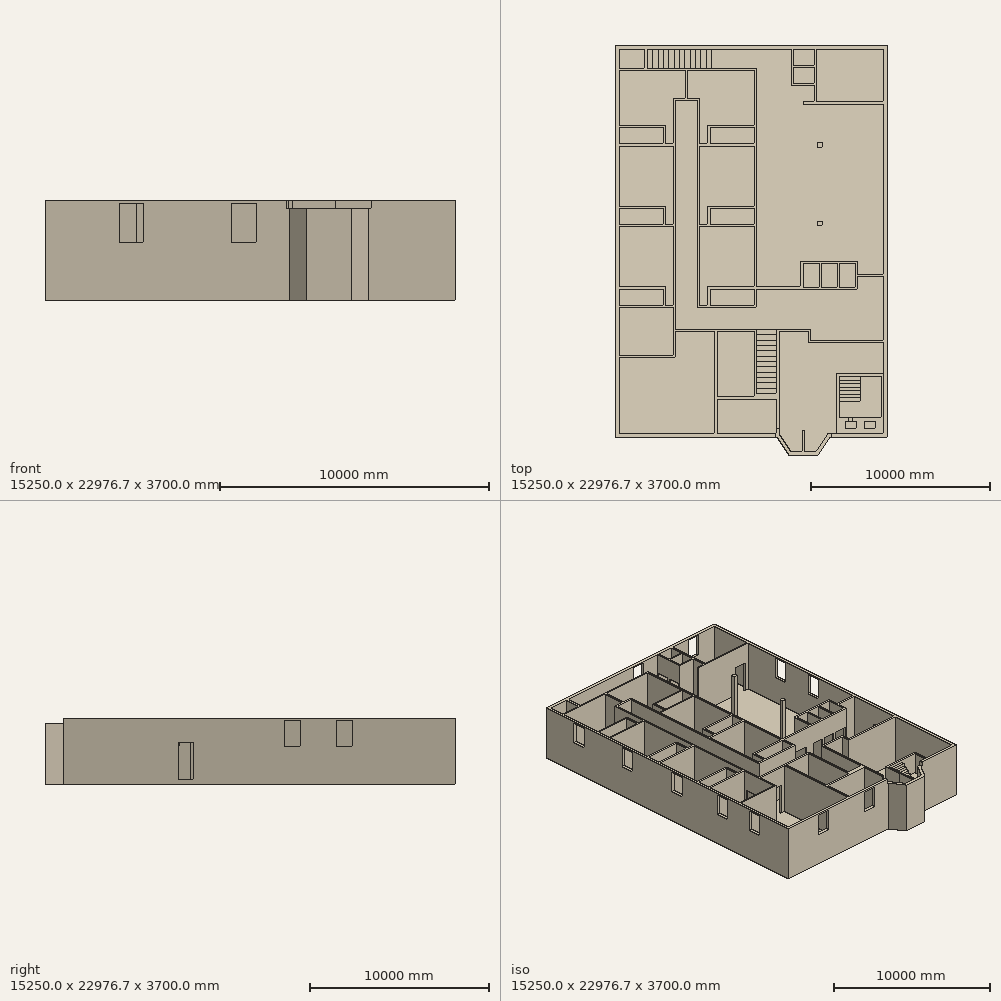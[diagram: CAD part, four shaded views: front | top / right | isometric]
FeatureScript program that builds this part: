
annotation { "Feature Type Name" : "Feature", "Feature Type Description" : "" }
export const myFeature = defineFeature(function(context is Context, id is Id, definition is map)
    precondition{}
    {
        {
            var Q0;
            Q0=qCreatedBy(makeId("Top.planeOp"),FACE);
            var sketch = newSketch(context, id + "F0", { "sketchPlane" : qUnion([Q0])});
            skLineSegment(sketch, "E0", {"start": v(-8625, -10471.67) * mm, "end": v(-8625, -7870.68) * mm});
            skLineSegment(sketch, "E1", {"start": v(-8625, 11488.33) * mm, "end": v(-949.17, 11488.33) * mm});
            skLineSegment(sketch, "E2", {"start": v(6625, 11488.33) * mm, "end": v(6625, 5731.46) * mm});
            skLineSegment(sketch, "E3", {"start": v(6625, -10471.67) * mm, "end": v(3405.76, -10471.67) * mm});
            skLineSegment(sketch, "E4", {"start": v(-8421.67, -10268.33) * mm, "end": v(-8421.67, -7870.68) * mm});
            skLineSegment(sketch, "E5", {"start": v(6421.67, 11285) * mm, "end": v(6421.67, 8336.67) * mm});
            skLineSegment(sketch, "E6", {"start": v(6421.67, -10268.33) * mm, "end": v(3295.42, -10268.33) * mm});
            skLineSegment(sketch, "E7", {"start": v(550.42, -4549.58) * mm, "end": v(550.42, -10268.33) * mm});
            skLineSegment(sketch, "E8", {"start": v(2634.58, -11285) * mm, "end": v(1973.75, -11285) * mm});
            skLineSegment(sketch, "E9", {"start": v(550.42, -10268.33) * mm, "end": v(1211.25, -11285) * mm});
            skLineSegment(sketch, "E10", {"start": v(3295.42, -10268.33) * mm, "end": v(2634.58, -11285) * mm});
            skLineSegment(sketch, "E11", {"start": v(440.07, -10471.67) * mm, "end": v(1100.9, -11488.33) * mm});
            skLineSegment(sketch, "E12", {"start": v(440.07, -10471.67) * mm, "end": v(-53.23, -10471.67) * mm});
            skLineSegment(sketch, "E13", {"start": v(2744.93, -11488.33) * mm, "end": v(1100.9, -11488.33) * mm});
            skLineSegment(sketch, "E14", {"start": v(423.33, -4422.5) * mm, "end": v(423.33, -8209.58) * mm});
            skLineSegment(sketch, "E15", {"start": v(1894.4, -2046.04) * mm, "end": v(1894.4, -724.38) * mm});
            skLineSegment(sketch, "E16", {"start": v(-720.42, -4422.5) * mm, "end": v(-720.42, -8209.58) * mm});
            skLineSegment(sketch, "E17", {"start": v(423.33, -8209.58) * mm, "end": v(-720.42, -8209.58) * mm});
            skLineSegment(sketch, "E18", {"start": v(423.33, -8336.67) * mm, "end": v(-1749.8, -8336.67) * mm});
            skLineSegment(sketch, "E19", {"start": v(-847.5, -4549.58) * mm, "end": v(-847.5, -8209.58) * mm});
            skLineSegment(sketch, "E20", {"start": v(423.33, -8336.67) * mm, "end": v(423.33, -10268.33) * mm});
            skLineSegment(sketch, "E21", {"start": v(-3046.04, -4549.58) * mm, "end": v(-3046.04, -10268.33) * mm});
            skLineSegment(sketch, "E22", {"start": v(-2918.96, -4549.58) * mm, "end": v(-2918.96, -8209.58) * mm});
            skLineSegment(sketch, "E23", {"start": v(-3046.04, -10268.33) * mm, "end": v(-4973.46, -10268.33) * mm});
            skLineSegment(sketch, "E24", {"start": v(-720.42, -4422.5) * mm, "end": v(-847.5, -4422.5) * mm});
            skLineSegment(sketch, "E25", {"start": v(-720.42, -3202.5) * mm, "end": v(-720.42, -2173.12) * mm});
            skLineSegment(sketch, "E26", {"start": v(-8421.67, 10192.08) * mm, "end": v(-720.42, 10192.08) * mm});
            skLineSegment(sketch, "E27", {"start": v(-8421.67, 10065) * mm, "end": v(-4698.12, 10065) * mm});
            skLineSegment(sketch, "E28", {"start": v(6421.67, -5159.58) * mm, "end": v(6421.67, -10268.33) * mm});
            skLineSegment(sketch, "E29", {"start": v(-8421.67, -3202.5) * mm, "end": v(-5371.67, -3202.5) * mm});
            skLineSegment(sketch, "E30", {"start": v(-847.5, -4422.5) * mm, "end": v(-1749.8, -4422.5) * mm});
            skLineSegment(sketch, "E31", {"start": v(-847.5, -4549.58) * mm, "end": v(-1749.8, -4549.58) * mm});
            skLineSegment(sketch, "E32", {"start": v(2634.58, 8336.67) * mm, "end": v(2634.58, 11285) * mm});
            skLineSegment(sketch, "E33", {"start": v(2507.5, 8336.67) * mm, "end": v(2507.5, 9251.67) * mm});
            skLineSegment(sketch, "E34", {"start": v(1351.04, 10268.33) * mm, "end": v(2507.5, 10268.33) * mm});
            skLineSegment(sketch, "E35", {"start": v(1351.04, 10370) * mm, "end": v(2507.5, 10370) * mm});
            skLineSegment(sketch, "E36", {"start": v(1351.04, 9353.33) * mm, "end": v(2507.5, 9353.33) * mm});
            skLineSegment(sketch, "E37", {"start": v(1249.38, 9251.67) * mm, "end": v(2507.5, 9251.67) * mm});
            skLineSegment(sketch, "E38", {"start": v(1897.5, 8336.67) * mm, "end": v(2507.5, 8336.67) * mm});
            skLineSegment(sketch, "E39", {"start": v(1897.5, 8209.58) * mm, "end": v(5252.5, 8209.58) * mm});
            skLineSegment(sketch, "E40", {"start": v(2634.58, 8336.67) * mm, "end": v(5252.5, 8336.67) * mm});
            skLineSegment(sketch, "E41", {"start": v(2507.5, 9353.33) * mm, "end": v(2507.5, 10268.33) * mm});
            skLineSegment(sketch, "E42", {"start": v(2507.5, 10370) * mm, "end": v(2507.5, 11285) * mm});
            skLineSegment(sketch, "E43", {"start": v(1351.04, 10268.33) * mm, "end": v(1351.04, 10242.92) * mm});
            skLineSegment(sketch, "E44", {"start": v(2634.58, 11285) * mm, "end": v(4070.62, 11285) * mm});
            skLineSegment(sketch, "E45", {"start": v(1351.04, 11285) * mm, "end": v(2507.5, 11285) * mm});
            skLineSegment(sketch, "E46", {"start": v(-34.17, 11285) * mm, "end": v(1249.38, 11285) * mm});
            skLineSegment(sketch, "E47", {"start": v(-8421.67, 11285) * mm, "end": v(-949.17, 11285) * mm});
            skLineSegment(sketch, "E48", {"start": v(-720.42, -4422.5) * mm, "end": v(423.33, -4422.5) * mm, "construction": true});
            skLineSegment(sketch, "E49", {"start": v(-720.42, -4727.5) * mm, "end": v(423.33, -4727.5) * mm, "construction": true});
            skLineSegment(sketch, "E50", {"start": v(-720.42, -5032.5) * mm, "end": v(423.33, -5032.5) * mm, "construction": true});
            skLineSegment(sketch, "E51", {"start": v(-720.42, -5337.5) * mm, "end": v(423.33, -5337.5) * mm, "construction": true});
            skLineSegment(sketch, "E52", {"start": v(-720.42, -5642.5) * mm, "end": v(423.33, -5642.5) * mm, "construction": true});
            skLineSegment(sketch, "E53", {"start": v(-720.42, -5947.5) * mm, "end": v(423.33, -5947.5) * mm, "construction": true});
            skLineSegment(sketch, "E54", {"start": v(-720.42, -6252.5) * mm, "end": v(423.33, -6252.5) * mm, "construction": true});
            skLineSegment(sketch, "E55", {"start": v(-720.42, -6557.5) * mm, "end": v(423.33, -6557.5) * mm, "construction": true});
            skLineSegment(sketch, "E56", {"start": v(-720.42, -6862.5) * mm, "end": v(423.33, -6862.5) * mm, "construction": true});
            skLineSegment(sketch, "E57", {"start": v(-720.42, -7167.5) * mm, "end": v(423.33, -7167.5) * mm, "construction": true});
            skLineSegment(sketch, "E58", {"start": v(-720.42, -7472.5) * mm, "end": v(423.33, -7472.5) * mm, "construction": true});
            skLineSegment(sketch, "E59", {"start": v(-720.42, -7777.5) * mm, "end": v(423.33, -7777.5) * mm, "construction": true});
            skLineSegment(sketch, "E60", {"start": v(-720.42, -8082.5) * mm, "end": v(423.33, -8082.5) * mm, "construction": true});
            skLineSegment(sketch, "E61", {"start": v(-148.54, -4422.5) * mm, "end": v(-148.54, -7472.5) * mm, "construction": true});
            skLineSegment(sketch, "E62", {"start": v(-148.54, -7472.5) * mm, "end": v(-241.29, -7340.69) * mm, "construction": true});
            skLineSegment(sketch, "E63", {"start": v(-148.54, -7472.5) * mm, "end": v(-72.14, -7345.97) * mm, "construction": true});
            skLineSegment(sketch, "E64", {"start": v(931.67, -4549.58) * mm, "end": v(931.67, -4422.5) * mm});
            skLineSegment(sketch, "E65", {"start": v(1795.83, -4549.58) * mm, "end": v(1795.83, -4422.5) * mm});
            skLineSegment(sketch, "E66", {"start": v(931.67, -4549.58) * mm, "end": v(550.42, -4549.58) * mm});
            skLineSegment(sketch, "E67", {"start": v(931.67, -4422.5) * mm, "end": v(423.33, -4422.5) * mm});
            skLineSegment(sketch, "E68", {"start": v(-720.42, -2173.12) * mm, "end": v(-377.3, -2173.12) * mm});
            skLineSegment(sketch, "E69", {"start": v(1351.04, 11285) * mm, "end": v(1351.04, 11259.58) * mm});
            skLineSegment(sketch, "E70", {"start": v(1249.38, 11285) * mm, "end": v(1249.38, 11259.58) * mm});
            skLineSegment(sketch, "E71", {"start": v(-3046.04, -4549.58) * mm, "end": v(-3351.04, -4549.58) * mm});
            skLineSegment(sketch, "E72", {"start": v(-2613.96, -4549.58) * mm, "end": v(-2613.96, -4422.5) * mm});
            skLineSegment(sketch, "E73", {"start": v(-2613.96, -4549.58) * mm, "end": v(-2918.96, -4549.58) * mm});
            skLineSegment(sketch, "E74", {"start": v(-2613.96, -4422.5) * mm, "end": v(-3351.04, -4422.5) * mm});
            skLineSegment(sketch, "E75", {"start": v(1795.83, -4549.58) * mm, "end": v(2177.08, -4549.58) * mm});
            skLineSegment(sketch, "E76", {"start": v(2809.4, -2046.04) * mm, "end": v(2809.4, -724.38) * mm});
            skLineSegment(sketch, "E77", {"start": v(2911.06, -2046.04) * mm, "end": v(2911.06, -724.38) * mm});
            skLineSegment(sketch, "E78", {"start": v(3826.06, -2046.04) * mm, "end": v(3826.06, -724.38) * mm});
            skLineSegment(sketch, "E79", {"start": v(3927.72, -2046.04) * mm, "end": v(3927.72, -724.38) * mm});
            skLineSegment(sketch, "E80", {"start": v(4842.72, -2046.04) * mm, "end": v(4842.72, -724.38) * mm});
            skLineSegment(sketch, "E81", {"start": v(4944.4, -2173.12) * mm, "end": v(4944.4, -1448.75) * mm});
            skLineSegment(sketch, "E82", {"start": v(3826.06, -2046.04) * mm, "end": v(3800.64, -2046.04) * mm});
            skLineSegment(sketch, "E83", {"start": v(4842.72, -2046.04) * mm, "end": v(4817.3, -2046.04) * mm});
            skLineSegment(sketch, "E84", {"start": v(2809.4, -2046.04) * mm, "end": v(2783.97, -2046.04) * mm});
            skLineSegment(sketch, "E85", {"start": v(3953.14, -2046.04) * mm, "end": v(3953.14, -2173.12) * mm});
            skLineSegment(sketch, "E86", {"start": v(4817.3, -2046.04) * mm, "end": v(4817.3, -2173.12) * mm});
            skLineSegment(sketch, "E87", {"start": v(2936.47, -2046.04) * mm, "end": v(2936.47, -2173.12) * mm});
            skLineSegment(sketch, "E88", {"start": v(3800.64, -2046.04) * mm, "end": v(3800.64, -2173.12) * mm});
            skLineSegment(sketch, "E89", {"start": v(1919.8, -2046.04) * mm, "end": v(1919.8, -2173.12) * mm});
            skLineSegment(sketch, "E90", {"start": v(2783.97, -2046.04) * mm, "end": v(2783.97, -2173.12) * mm});
            skLineSegment(sketch, "E91", {"start": v(1919.8, -2046.04) * mm, "end": v(1894.4, -2046.04) * mm});
            skLineSegment(sketch, "E92", {"start": v(2783.97, -2173.12) * mm, "end": v(2936.47, -2173.12) * mm});
            skLineSegment(sketch, "E93", {"start": v(2936.47, -2046.04) * mm, "end": v(2911.06, -2046.04) * mm});
            skLineSegment(sketch, "E94", {"start": v(3800.64, -2173.12) * mm, "end": v(3953.14, -2173.12) * mm});
            skLineSegment(sketch, "E95", {"start": v(3953.14, -2046.04) * mm, "end": v(3927.72, -2046.04) * mm});
            skLineSegment(sketch, "E96", {"start": v(4817.3, -2173.12) * mm, "end": v(4944.4, -2173.12) * mm});
            skLineSegment(sketch, "E97", {"start": v(2304.17, -4422.5) * mm, "end": v(1795.83, -4422.5) * mm});
            skLineSegment(sketch, "E98", {"start": v(1249.38, 9378.75) * mm, "end": v(1351.04, 9378.75) * mm});
            skLineSegment(sketch, "E99", {"start": v(1249.38, 10242.92) * mm, "end": v(1351.04, 10242.92) * mm});
            skLineSegment(sketch, "E100", {"start": v(1249.38, 10395.42) * mm, "end": v(1351.04, 10395.42) * mm});
            skLineSegment(sketch, "E101", {"start": v(1249.38, 11259.58) * mm, "end": v(1351.04, 11259.58) * mm});
            skLineSegment(sketch, "E102", {"start": v(1351.04, 10395.42) * mm, "end": v(1351.04, 10370) * mm});
            skLineSegment(sketch, "E103", {"start": v(1249.38, 10395.42) * mm, "end": v(1249.38, 10242.92) * mm});
            skLineSegment(sketch, "E104", {"start": v(1351.04, 9378.75) * mm, "end": v(1351.04, 9353.33) * mm});
            skLineSegment(sketch, "E105", {"start": v(1249.38, 9378.75) * mm, "end": v(1249.38, 9251.67) * mm});
            skLineSegment(sketch, "E106", {"start": v(-5244.58, -4422.5) * mm, "end": v(-5244.58, -4244.58) * mm});
            skLineSegment(sketch, "E107", {"start": v(-5371.67, -3202.5) * mm, "end": v(-5371.67, -3380.42) * mm});
            skLineSegment(sketch, "E108", {"start": v(-5371.67, -3380.42) * mm, "end": v(-5244.58, -3380.42) * mm});
            skLineSegment(sketch, "E109", {"start": v(-5371.67, -4244.58) * mm, "end": v(-5244.58, -4244.58) * mm});
            skLineSegment(sketch, "E110", {"start": v(-5244.58, -3380.42) * mm, "end": v(-5244.58, -1575.83) * mm});
            skLineSegment(sketch, "E111", {"start": v(-5371.67, -4244.58) * mm, "end": v(-5371.67, -4422.5) * mm});
            skLineSegment(sketch, "E112", {"start": v(-5371.67, -3380.42) * mm, "end": v(-5371.67, -3202.5) * mm});
            skLineSegment(sketch, "E113", {"start": v(-3351.04, -4549.58) * mm, "end": v(-3351.04, -4422.5) * mm});
            skLineSegment(sketch, "E114", {"start": v(-4215.2, -4549.58) * mm, "end": v(-5244.58, -4549.58) * mm});
            skLineSegment(sketch, "E115", {"start": v(-4215.2, -4422.5) * mm, "end": v(-5244.58, -4422.5) * mm});
            skLineSegment(sketch, "E116", {"start": v(-1749.8, -4549.58) * mm, "end": v(-1749.8, -4422.5) * mm});
            skLineSegment(sketch, "E117", {"start": v(-4215.2, -4549.58) * mm, "end": v(-4215.2, -4422.5) * mm});
            skLineSegment(sketch, "E118", {"start": v(-8421.67, 7015) * mm, "end": v(-8421.67, 8082.5) * mm});
            skLineSegment(sketch, "E119", {"start": v(-3897.5, 5845.83) * mm, "end": v(-847.5, 5845.83) * mm});
            skLineSegment(sketch, "E120", {"start": v(-847.5, 7015) * mm, "end": v(-847.5, 10065) * mm});
            skLineSegment(sketch, "E121", {"start": v(-4571.04, 10065) * mm, "end": v(-847.5, 10065) * mm});
            skLineSegment(sketch, "E122", {"start": v(-5244.58, 8400.2) * mm, "end": v(-4024.58, 8400.2) * mm});
            skLineSegment(sketch, "E123", {"start": v(-5371.67, 8527.3) * mm, "end": v(-4698.12, 8527.3) * mm});
            skLineSegment(sketch, "E124", {"start": v(-4024.58, 8400.2) * mm, "end": v(-4024.58, 8311.25) * mm});
            skLineSegment(sketch, "E125", {"start": v(-3897.5, 8311.25) * mm, "end": v(-3897.5, 8527.3) * mm});
            skLineSegment(sketch, "E126", {"start": v(-4024.58, -3202.5) * mm, "end": v(-720.42, -3202.5) * mm});
            skLineSegment(sketch, "E127", {"start": v(6421.67, 8209.58) * mm, "end": v(6421.67, 5731.46) * mm});
            skLineSegment(sketch, "E128", {"start": v(6116.67, 8336.67) * mm, "end": v(6116.67, 8209.58) * mm});
            skLineSegment(sketch, "E129", {"start": v(6116.67, 8336.67) * mm, "end": v(6421.67, 8336.67) * mm});
            skLineSegment(sketch, "E130", {"start": v(6116.67, 8209.58) * mm, "end": v(6421.67, 8209.58) * mm});
            skLineSegment(sketch, "E131", {"start": v(1351.04, -2033.33) * mm, "end": v(1767.3, -2033.33) * mm});
            skLineSegment(sketch, "E132", {"start": v(-720.42, -2033.33) * mm, "end": v(-720.42, 10192.08) * mm});
            skLineSegment(sketch, "E133", {"start": v(-377.3, -2173.12) * mm, "end": v(-377.3, -2033.33) * mm});
            skLineSegment(sketch, "E134", {"start": v(6421.67, -3170.73) * mm, "end": v(6625, -3170.73) * mm});
            skLineSegment(sketch, "E135", {"start": v(6421.67, -4034.9) * mm, "end": v(6625, -4034.9) * mm});
            skLineSegment(sketch, "E136", {"start": v(6625, -4034.9) * mm, "end": v(6625, -10471.67) * mm});
            skLineSegment(sketch, "E137", {"start": v(6421.67, -4034.9) * mm, "end": v(6421.67, -5032.5) * mm});
            skLineSegment(sketch, "E138", {"start": v(-3236.67, 10192.08) * mm, "end": v(-3236.67, 11285) * mm, "construction": true});
            skLineSegment(sketch, "E139", {"start": v(-8421.67, 10192.08) * mm, "end": v(-8421.67, 11285) * mm});
            skLineSegment(sketch, "E140", {"start": v(-3541.67, 10192.08) * mm, "end": v(-3541.67, 11285) * mm, "construction": true});
            skLineSegment(sketch, "E141", {"start": v(-3846.67, 10192.08) * mm, "end": v(-3846.67, 11285) * mm, "construction": true});
            skLineSegment(sketch, "E142", {"start": v(-4151.67, 10192.08) * mm, "end": v(-4151.67, 11285) * mm, "construction": true});
            skLineSegment(sketch, "E143", {"start": v(-4456.67, 10192.08) * mm, "end": v(-4456.67, 11285) * mm, "construction": true});
            skLineSegment(sketch, "E144", {"start": v(-4761.67, 10192.08) * mm, "end": v(-4761.67, 11285) * mm, "construction": true});
            skLineSegment(sketch, "E145", {"start": v(-5066.67, 10192.08) * mm, "end": v(-5066.67, 11285) * mm, "construction": true});
            skLineSegment(sketch, "E146", {"start": v(-5371.67, 10192.08) * mm, "end": v(-5371.67, 11285) * mm, "construction": true});
            skLineSegment(sketch, "E147", {"start": v(-5676.67, 10192.08) * mm, "end": v(-5676.67, 11285) * mm, "construction": true});
            skLineSegment(sketch, "E148", {"start": v(-5981.67, 10192.08) * mm, "end": v(-5981.67, 11285) * mm, "construction": true});
            skLineSegment(sketch, "E149", {"start": v(-6286.67, 10192.08) * mm, "end": v(-6286.67, 11285) * mm, "construction": true});
            skLineSegment(sketch, "E150", {"start": v(-6591.67, 10192.08) * mm, "end": v(-6591.67, 11285) * mm, "construction": true});
            skLineSegment(sketch, "E151", {"start": v(-6896.67, 10192.08) * mm, "end": v(-6896.67, 11285) * mm, "construction": true});
            skLineSegment(sketch, "E152", {"start": v(-7201.67, 10192.08) * mm, "end": v(-7201.67, 11285) * mm, "construction": true});
            skLineSegment(sketch, "E153", {"start": v(-3236.67, 10738.54) * mm, "end": v(-7201.67, 10738.54) * mm, "construction": true});
            skLineSegment(sketch, "E154", {"start": v(-7201.67, 10738.54) * mm, "end": v(-7003.23, 10858.23) * mm, "construction": true});
            skLineSegment(sketch, "E155", {"start": v(-7201.67, 10738.54) * mm, "end": v(-7003.23, 10618.85) * mm, "construction": true});
            skLineSegment(sketch, "E156", {"start": v(1872.08, -10065) * mm, "end": v(1872.08, -11285) * mm});
            skLineSegment(sketch, "E157", {"start": v(1973.75, -10065) * mm, "end": v(1973.75, -11285) * mm});
            skLineSegment(sketch, "E158", {"start": v(1872.08, -10065) * mm, "end": v(1973.75, -10065) * mm});
            skLineSegment(sketch, "E159", {"start": v(1872.08, -11285) * mm, "end": v(1211.25, -11285) * mm});
            skLineSegment(sketch, "E160", {"start": v(2177.08, -4549.58) * mm, "end": v(2177.08, -5159.58) * mm});
            skLineSegment(sketch, "E161", {"start": v(6421.67, -5032.5) * mm, "end": v(2304.17, -5032.5) * mm});
            skLineSegment(sketch, "E162", {"start": v(6421.67, -5159.58) * mm, "end": v(2177.08, -5159.58) * mm});
            skLineSegment(sketch, "E163", {"start": v(2304.17, -4422.5) * mm, "end": v(2304.17, -5032.5) * mm});
            skLineSegment(sketch, "E164", {"start": v(1767.3, -597.3) * mm, "end": v(4944.4, -597.3) * mm});
            skLineSegment(sketch, "E165", {"start": v(1894.4, -724.38) * mm, "end": v(2809.4, -724.38) * mm});
            skLineSegment(sketch, "E166", {"start": v(4944.4, -1321.67) * mm, "end": v(6421.67, -1321.67) * mm});
            skLineSegment(sketch, "E167", {"start": v(4944.4, -1448.75) * mm, "end": v(6421.67, -1448.75) * mm});
            skLineSegment(sketch, "E168", {"start": v(6421.67, -1448.75) * mm, "end": v(6421.67, -3170.73) * mm});
            skLineSegment(sketch, "E169", {"start": v(4944.4, -1321.67) * mm, "end": v(4944.4, -597.3) * mm});
            skLineSegment(sketch, "E170", {"start": v(1767.3, -2033.33) * mm, "end": v(1767.3, -597.3) * mm});
            skLineSegment(sketch, "E171", {"start": v(1351.04, -2033.33) * mm, "end": v(1351.04, -2173.12) * mm});
            skLineSegment(sketch, "E172", {"start": v(2911.06, -724.38) * mm, "end": v(3826.06, -724.38) * mm});
            skLineSegment(sketch, "E173", {"start": v(3927.72, -724.38) * mm, "end": v(4842.72, -724.38) * mm});
            skLineSegment(sketch, "E174", {"start": v(-5371.67, 8311.25) * mm, "end": v(-5244.58, 8311.25) * mm});
            skLineSegment(sketch, "E175", {"start": v(-5244.58, 8311.25) * mm, "end": v(-5244.58, 8400.2) * mm});
            skLineSegment(sketch, "E176", {"start": v(-5371.67, 8311.25) * mm, "end": v(-5371.67, 8527.3) * mm});
            skLineSegment(sketch, "E177", {"start": v(-3897.5, 8311.25) * mm, "end": v(-4024.58, 8311.25) * mm});
            skLineSegment(sketch, "E178", {"start": v(-847.5, -3075.42) * mm, "end": v(-3312.92, -3075.42) * mm});
            skLineSegment(sketch, "E179", {"start": v(-847.5, -2033.33) * mm, "end": v(-847.5, 1321.67) * mm});
            skLineSegment(sketch, "E180", {"start": v(-847.5, -3075.42) * mm, "end": v(-847.5, -2160.42) * mm});
            skLineSegment(sketch, "E181", {"start": v(-3897.5, -3075.42) * mm, "end": v(-3897.5, -2160.42) * mm});
            skLineSegment(sketch, "E182", {"start": v(-847.5, 1321.67) * mm, "end": v(-3897.5, 1321.67) * mm});
            skLineSegment(sketch, "E183", {"start": v(-847.5, 2490.83) * mm, "end": v(-847.5, 5845.83) * mm});
            skLineSegment(sketch, "E184", {"start": v(-847.5, 5845.83) * mm, "end": v(-3897.5, 5845.83) * mm});
            skLineSegment(sketch, "E185", {"start": v(-3897.5, -711.67) * mm, "end": v(-4024.58, -711.67) * mm});
            skLineSegment(sketch, "E186", {"start": v(-3897.5, -1575.83) * mm, "end": v(-4024.58, -1575.83) * mm});
            skLineSegment(sketch, "E187", {"start": v(-3897.5, -711.67) * mm, "end": v(-3897.5, 1321.67) * mm});
            skLineSegment(sketch, "E188", {"start": v(-3897.5, -3075.42) * mm, "end": v(-3897.5, -1575.83) * mm});
            skLineSegment(sketch, "E189", {"start": v(-3897.5, 3812.5) * mm, "end": v(-4024.58, 3812.5) * mm});
            skLineSegment(sketch, "E190", {"start": v(-4024.58, -3202.5) * mm, "end": v(-4024.58, -1575.83) * mm});
            skLineSegment(sketch, "E191", {"start": v(-4024.58, -711.67) * mm, "end": v(-4024.58, 2948.33) * mm});
            skLineSegment(sketch, "E192", {"start": v(-4024.58, 3812.5) * mm, "end": v(-4024.58, 7447.08) * mm});
            skLineSegment(sketch, "E193", {"start": v(-3897.5, 3812.5) * mm, "end": v(-3897.5, 5845.83) * mm});
            skLineSegment(sketch, "E194", {"start": v(5252.5, 8336.67) * mm, "end": v(5252.5, 8209.58) * mm});
            skLineSegment(sketch, "E195", {"start": v(440.07, -10471.67) * mm, "end": v(-790.31, -10471.67) * mm});
            skLineSegment(sketch, "E196", {"start": v(423.33, -10268.33) * mm, "end": v(-790.31, -10268.33) * mm});
            skLineSegment(sketch, "E197", {"start": v(2723.54, 1385.2) * mm, "end": v(2723.54, 1639.38) * mm});
            skLineSegment(sketch, "E198", {"start": v(2977.7, 1385.2) * mm, "end": v(2977.7, 1639.38) * mm});
            skLineSegment(sketch, "E199", {"start": v(2723.54, 6036.46) * mm, "end": v(2977.7, 6036.46) * mm});
            skLineSegment(sketch, "E200", {"start": v(2723.54, 5782.3) * mm, "end": v(2977.7, 5782.3) * mm});
            skLineSegment(sketch, "E201", {"start": v(2977.7, 5782.3) * mm, "end": v(2977.7, 6036.46) * mm});
            skLineSegment(sketch, "E202", {"start": v(2723.54, 5782.3) * mm, "end": v(2723.54, 6036.46) * mm});
            skLineSegment(sketch, "E203", {"start": v(2723.54, 1639.38) * mm, "end": v(2977.7, 1639.38) * mm});
            skLineSegment(sketch, "E204", {"start": v(2723.54, 1385.2) * mm, "end": v(2977.7, 1385.2) * mm});
            skLineSegment(sketch, "E205", {"start": v(1897.5, 8336.67) * mm, "end": v(1897.5, 8209.58) * mm});
            skLineSegment(sketch, "E206", {"start": v(-4698.12, 8527.3) * mm, "end": v(-4698.12, 10065) * mm});
            skLineSegment(sketch, "E207", {"start": v(-4571.04, 8527.3) * mm, "end": v(-4571.04, 10065) * mm});
            skLineSegment(sketch, "E208", {"start": v(-4571.04, 8527.3) * mm, "end": v(-3897.5, 8527.3) * mm});
            skLineSegment(sketch, "E209", {"start": v(-847.5, -2160.42) * mm, "end": v(-1965.83, -2160.42) * mm});
            skLineSegment(sketch, "E210", {"start": v(-3312.92, -3075.42) * mm, "end": v(-3312.92, -2160.42) * mm});
            skLineSegment(sketch, "E211", {"start": v(-1965.83, -2160.42) * mm, "end": v(-1965.83, -2033.33) * mm});
            skLineSegment(sketch, "E212", {"start": v(-3440, -2033.33) * mm, "end": v(-3440, -3075.42) * mm});
            skLineSegment(sketch, "E213", {"start": v(-847.5, -2033.33) * mm, "end": v(-1965.83, -2033.33) * mm});
            skLineSegment(sketch, "E214", {"start": v(4858.54, -7065.83) * mm, "end": v(4858.54, -8285.83) * mm, "construction": true});
            skLineSegment(sketch, "E215", {"start": v(4858.54, -7370.83) * mm, "end": v(3905.42, -7370.83) * mm, "construction": true});
            skLineSegment(sketch, "E216", {"start": v(4858.54, -7675.83) * mm, "end": v(3905.42, -7675.83) * mm, "construction": true});
            skLineSegment(sketch, "E217", {"start": v(4858.54, -7980.83) * mm, "end": v(3905.42, -7980.83) * mm, "construction": true});
            skLineSegment(sketch, "E218", {"start": v(4858.54, -8285.83) * mm, "end": v(3905.42, -8285.83) * mm, "construction": true});
            skLineSegment(sketch, "E219", {"start": v(4381.98, -8285.83) * mm, "end": v(4381.98, -7370.83) * mm, "construction": true});
            skLineSegment(sketch, "E220", {"start": v(4381.98, -7370.83) * mm, "end": v(4254.51, -7542.45) * mm, "construction": true});
            skLineSegment(sketch, "E221", {"start": v(4381.98, -7370.83) * mm, "end": v(4509.45, -7542.45) * mm, "construction": true});
            skLineSegment(sketch, "E222", {"start": v(6269.17, -9353.33) * mm, "end": v(6269.17, -7065.83) * mm, "construction": true});
            skLineSegment(sketch, "E223", {"start": v(6269.17, -7065.83) * mm, "end": v(3905.42, -7065.83) * mm, "construction": true});
            skLineSegment(sketch, "E224", {"start": v(3905.42, -7065.83) * mm, "end": v(3905.42, -9353.33) * mm, "construction": true});
            skLineSegment(sketch, "E225", {"start": v(3905.42, -9353.33) * mm, "end": v(6269.17, -9353.33) * mm, "construction": true});
            skLineSegment(sketch, "E226", {"start": v(5319.36, -9707.45) * mm, "end": v(5319.36, -10063.28) * mm, "construction": true});
            skLineSegment(sketch, "E227", {"start": v(5929.36, -9707.45) * mm, "end": v(5929.36, -10063.28) * mm, "construction": true});
            skLineSegment(sketch, "E228", {"start": v(5929.36, -9707.45) * mm, "end": v(5319.36, -9707.45) * mm, "construction": true});
            skLineSegment(sketch, "E229", {"start": v(5929.36, -10063.28) * mm, "end": v(5319.36, -10063.28) * mm, "construction": true});
            skLineSegment(sketch, "E230", {"start": v(4448.56, -9707.45) * mm, "end": v(4448.56, -9353.33) * mm, "construction": true});
            skLineSegment(sketch, "E231", {"start": v(4651.9, -9707.45) * mm, "end": v(4651.9, -9353.33) * mm, "construction": true});
            skLineSegment(sketch, "E232", {"start": v(4245.23, -9707.45) * mm, "end": v(4448.56, -9707.45) * mm, "construction": true});
            skLineSegment(sketch, "E233", {"start": v(4651.9, -9707.45) * mm, "end": v(4855.23, -9707.45) * mm, "construction": true});
            skLineSegment(sketch, "E234", {"start": v(4855.23, -9707.45) * mm, "end": v(4855.23, -10063.28) * mm, "construction": true});
            skLineSegment(sketch, "E235", {"start": v(3752.92, -10268.33) * mm, "end": v(6396.25, -10268.33) * mm});
            skLineSegment(sketch, "E236", {"start": v(4245.23, -9707.45) * mm, "end": v(4245.23, -10063.28) * mm, "construction": true});
            skLineSegment(sketch, "E237", {"start": v(4245.23, -10063.28) * mm, "end": v(4855.23, -10063.28) * mm, "construction": true});
            skLineSegment(sketch, "E238", {"start": v(6421.67, -9505.83) * mm, "end": v(6421.67, -6913.33) * mm});
            skLineSegment(sketch, "E239", {"start": v(3752.92, -6913.33) * mm, "end": v(3752.92, -10268.33) * mm, "construction": true});
            skLineSegment(sketch, "E240", {"start": v(6421.67, -6913.33) * mm, "end": v(3752.92, -6913.33) * mm, "construction": true});
            skLineSegment(sketch, "E241", {"start": v(3405.76, -10471.67) * mm, "end": v(2744.93, -11488.33) * mm});
            skLineSegment(sketch, "E242", {"start": v(-8421.67, 8082.5) * mm, "end": v(-8625, 8082.5) * mm});
            skLineSegment(sketch, "E243", {"start": v(-8421.67, 8997.5) * mm, "end": v(-8625, 8997.5) * mm});
            skLineSegment(sketch, "E244", {"start": v(-8421.67, 3710.83) * mm, "end": v(-8625, 3710.83) * mm});
            skLineSegment(sketch, "E245", {"start": v(-8421.67, 4625.83) * mm, "end": v(-8625, 4625.83) * mm});
            skLineSegment(sketch, "E246", {"start": v(-8421.67, -3998.86) * mm, "end": v(-8625, -3998.86) * mm});
            skLineSegment(sketch, "E247", {"start": v(-8421.67, -4913.86) * mm, "end": v(-8625, -4913.86) * mm});
            skLineSegment(sketch, "E248", {"start": v(-8421.67, -7870.68) * mm, "end": v(-8625, -7870.68) * mm});
            skLineSegment(sketch, "E249", {"start": v(-8421.67, -6955.68) * mm, "end": v(-8625, -6955.68) * mm});
            skLineSegment(sketch, "E250", {"start": v(-5888.46, -10471.67) * mm, "end": v(-5888.46, -10268.33) * mm});
            skLineSegment(sketch, "E251", {"start": v(-4973.46, -10471.67) * mm, "end": v(-4973.46, -10268.33) * mm});
            skLineSegment(sketch, "E252", {"start": v(6421.67, 4816.46) * mm, "end": v(6625, 4816.46) * mm});
            skLineSegment(sketch, "E253", {"start": v(6421.67, 5731.46) * mm, "end": v(6625, 5731.46) * mm});
            skLineSegment(sketch, "E254", {"start": v(4070.62, 11285) * mm, "end": v(4070.62, 11488.33) * mm});
            skLineSegment(sketch, "E255", {"start": v(4985.62, 11285) * mm, "end": v(4985.62, 11488.33) * mm});
            skLineSegment(sketch, "E256", {"start": v(-949.17, 11285) * mm, "end": v(-949.17, 11488.33) * mm});
            skLineSegment(sketch, "E257", {"start": v(-34.17, 11285) * mm, "end": v(-34.17, 11488.33) * mm});
            skLineSegment(sketch, "E258", {"start": v(-5888.46, -10471.67) * mm, "end": v(-8625, -10471.67) * mm});
            skLineSegment(sketch, "E259", {"start": v(-5888.46, -10268.33) * mm, "end": v(-8421.67, -10268.33) * mm});
            skLineSegment(sketch, "E260", {"start": v(-8421.67, -6955.68) * mm, "end": v(-8421.67, -5998.3) * mm});
            skLineSegment(sketch, "E261", {"start": v(-8625, -6955.68) * mm, "end": v(-8625, -4913.86) * mm});
            skLineSegment(sketch, "E262", {"start": v(-8421.67, -3998.86) * mm, "end": v(-8421.67, -3202.5) * mm});
            skLineSegment(sketch, "E263", {"start": v(-8625, -3998.86) * mm, "end": v(-8625, -813.33) * mm});
            skLineSegment(sketch, "E264", {"start": v(-8625, 4625.83) * mm, "end": v(-8625, 8082.5) * mm});
            skLineSegment(sketch, "E265", {"start": v(-8421.67, -813.33) * mm, "end": v(-8625, -813.33) * mm});
            skLineSegment(sketch, "E266", {"start": v(-8421.67, 101.67) * mm, "end": v(-8625, 101.67) * mm});
            skLineSegment(sketch, "E267", {"start": v(-8625, 101.67) * mm, "end": v(-8625, 3710.83) * mm});
            skLineSegment(sketch, "E268", {"start": v(-8421.67, 8997.5) * mm, "end": v(-8421.67, 10065) * mm});
            skLineSegment(sketch, "E269", {"start": v(-8625, 8997.5) * mm, "end": v(-8625, 11488.33) * mm});
            skLineSegment(sketch, "E270", {"start": v(-34.17, 11488.33) * mm, "end": v(4070.62, 11488.33) * mm});
            skLineSegment(sketch, "E271", {"start": v(4985.62, 11285) * mm, "end": v(6421.67, 11285) * mm});
            skLineSegment(sketch, "E272", {"start": v(4985.62, 11488.33) * mm, "end": v(6625, 11488.33) * mm});
            skLineSegment(sketch, "E273", {"start": v(6625, 4816.46) * mm, "end": v(6625, 2795.83) * mm});
            skLineSegment(sketch, "E274", {"start": v(6421.67, 4816.46) * mm, "end": v(6421.67, 2795.83) * mm});
            skLineSegment(sketch, "E275", {"start": v(6625, 1880.83) * mm, "end": v(6625, -3170.73) * mm});
            skLineSegment(sketch, "E276", {"start": v(6421.67, 1880.83) * mm, "end": v(6421.67, -1321.67) * mm});
            skLineSegment(sketch, "E277", {"start": v(-2830, -2033.33) * mm, "end": v(-3440, -2033.33) * mm});
            skLineSegment(sketch, "E278", {"start": v(-3440, -3075.42) * mm, "end": v(-3897.5, -3075.42) * mm});
            skLineSegment(sketch, "E279", {"start": v(-847.5, 1448.75) * mm, "end": v(-847.5, 2363.75) * mm});
            skLineSegment(sketch, "E280", {"start": v(-3897.5, 1448.75) * mm, "end": v(-3897.5, 2363.75) * mm});
            skLineSegment(sketch, "E281", {"start": v(-3897.5, 2948.33) * mm, "end": v(-4024.58, 2948.33) * mm});
            skLineSegment(sketch, "E282", {"start": v(-3897.5, 1448.75) * mm, "end": v(-3897.5, 2948.33) * mm});
            skLineSegment(sketch, "E283", {"start": v(-847.5, 2363.75) * mm, "end": v(-1965.83, 2363.75) * mm});
            skLineSegment(sketch, "E284", {"start": v(-1965.83, 2363.75) * mm, "end": v(-1965.83, 2490.83) * mm});
            skLineSegment(sketch, "E285", {"start": v(-847.5, 2490.83) * mm, "end": v(-1965.83, 2490.83) * mm});
            skLineSegment(sketch, "E286", {"start": v(-3440, 1448.75) * mm, "end": v(-3897.5, 1448.75) * mm});
            skLineSegment(sketch, "E287", {"start": v(-847.5, 1448.75) * mm, "end": v(-3312.92, 1448.75) * mm});
            skLineSegment(sketch, "E288", {"start": v(-847.5, 5972.92) * mm, "end": v(-847.5, 6887.92) * mm});
            skLineSegment(sketch, "E289", {"start": v(-3897.5, 5972.92) * mm, "end": v(-3897.5, 6887.92) * mm});
            skLineSegment(sketch, "E290", {"start": v(-3897.5, 7447.08) * mm, "end": v(-4024.58, 7447.08) * mm});
            skLineSegment(sketch, "E291", {"start": v(-3897.5, 5972.92) * mm, "end": v(-3897.5, 7447.08) * mm});
            skLineSegment(sketch, "E292", {"start": v(-847.5, 6887.92) * mm, "end": v(-1965.83, 6887.92) * mm});
            skLineSegment(sketch, "E293", {"start": v(-1965.83, 6887.92) * mm, "end": v(-1965.83, 7015) * mm});
            skLineSegment(sketch, "E294", {"start": v(-847.5, 7015) * mm, "end": v(-1965.83, 7015) * mm});
            skLineSegment(sketch, "E295", {"start": v(-3440, 5972.92) * mm, "end": v(-3897.5, 5972.92) * mm});
            skLineSegment(sketch, "E296", {"start": v(-847.5, 5972.92) * mm, "end": v(-3312.92, 5972.92) * mm});
            skLineSegment(sketch, "E297", {"start": v(-5371.67, 5845.83) * mm, "end": v(-8421.67, 5845.83) * mm});
            skLineSegment(sketch, "E298", {"start": v(-8421.67, -2033.33) * mm, "end": v(-8421.67, -813.33) * mm});
            skLineSegment(sketch, "E299", {"start": v(-8421.67, -3075.42) * mm, "end": v(-8421.67, -2160.42) * mm});
            skLineSegment(sketch, "E300", {"start": v(-5371.67, -3075.42) * mm, "end": v(-5371.67, -2160.42) * mm});
            skLineSegment(sketch, "E301", {"start": v(-8421.67, 1321.67) * mm, "end": v(-5371.67, 1321.67) * mm});
            skLineSegment(sketch, "E302", {"start": v(-8421.67, 2490.83) * mm, "end": v(-8421.67, 3710.83) * mm});
            skLineSegment(sketch, "E303", {"start": v(-8421.67, 5845.83) * mm, "end": v(-5371.67, 5845.83) * mm});
            skLineSegment(sketch, "E304", {"start": v(-5371.67, -711.67) * mm, "end": v(-5244.58, -711.67) * mm});
            skLineSegment(sketch, "E305", {"start": v(-5371.67, -1575.83) * mm, "end": v(-5244.58, -1575.83) * mm});
            skLineSegment(sketch, "E306", {"start": v(-5371.67, -711.67) * mm, "end": v(-5371.67, 1321.67) * mm});
            skLineSegment(sketch, "E307", {"start": v(-5371.67, -3075.42) * mm, "end": v(-5371.67, -1575.83) * mm});
            skLineSegment(sketch, "E308", {"start": v(-5371.67, 3812.5) * mm, "end": v(-5244.58, 3812.5) * mm});
            skLineSegment(sketch, "E309", {"start": v(-5244.58, -711.67) * mm, "end": v(-5244.58, 2948.33) * mm});
            skLineSegment(sketch, "E310", {"start": v(-5244.58, 3812.5) * mm, "end": v(-5244.58, 7447.08) * mm});
            skLineSegment(sketch, "E311", {"start": v(-5371.67, 3812.5) * mm, "end": v(-5371.67, 5845.83) * mm});
            skLineSegment(sketch, "E312", {"start": v(-8421.67, -2160.42) * mm, "end": v(-7303.33, -2160.42) * mm});
            skLineSegment(sketch, "E313", {"start": v(-7303.33, -2160.42) * mm, "end": v(-7303.33, -2033.33) * mm});
            skLineSegment(sketch, "E314", {"start": v(-8421.67, -2033.33) * mm, "end": v(-7303.33, -2033.33) * mm});
            skLineSegment(sketch, "E315", {"start": v(-6439.17, -2033.33) * mm, "end": v(-5829.17, -2033.33) * mm});
            skLineSegment(sketch, "E316", {"start": v(-5829.17, -2033.33) * mm, "end": v(-5829.17, -3075.42) * mm});
            skLineSegment(sketch, "E317", {"start": v(-5956.25, -3075.42) * mm, "end": v(-5956.25, -2160.42) * mm});
            skLineSegment(sketch, "E318", {"start": v(-5829.17, -3075.42) * mm, "end": v(-5371.67, -3075.42) * mm});
            skLineSegment(sketch, "E319", {"start": v(-8421.67, -3075.42) * mm, "end": v(-5956.25, -3075.42) * mm});
            skLineSegment(sketch, "E320", {"start": v(-8421.67, 1448.75) * mm, "end": v(-8421.67, 2363.75) * mm});
            skLineSegment(sketch, "E321", {"start": v(-5371.67, 1448.75) * mm, "end": v(-5371.67, 2363.75) * mm});
            skLineSegment(sketch, "E322", {"start": v(-5371.67, 2948.33) * mm, "end": v(-5244.58, 2948.33) * mm});
            skLineSegment(sketch, "E323", {"start": v(-5371.67, 1448.75) * mm, "end": v(-5371.67, 2948.33) * mm});
            skLineSegment(sketch, "E324", {"start": v(-8421.67, 2363.75) * mm, "end": v(-7303.33, 2363.75) * mm});
            skLineSegment(sketch, "E325", {"start": v(-7303.33, 2363.75) * mm, "end": v(-7303.33, 2490.83) * mm});
            skLineSegment(sketch, "E326", {"start": v(-8421.67, 2490.83) * mm, "end": v(-7303.33, 2490.83) * mm});
            skLineSegment(sketch, "E327", {"start": v(-5829.17, 1448.75) * mm, "end": v(-5371.67, 1448.75) * mm});
            skLineSegment(sketch, "E328", {"start": v(-8421.67, 1448.75) * mm, "end": v(-5956.25, 1448.75) * mm});
            skLineSegment(sketch, "E329", {"start": v(-8421.67, 5972.92) * mm, "end": v(-8421.67, 6887.92) * mm});
            skLineSegment(sketch, "E330", {"start": v(-5371.67, 5972.92) * mm, "end": v(-5371.67, 6887.92) * mm});
            skLineSegment(sketch, "E331", {"start": v(-5371.67, 7447.08) * mm, "end": v(-5244.58, 7447.08) * mm});
            skLineSegment(sketch, "E332", {"start": v(-5371.67, 5972.92) * mm, "end": v(-5371.67, 7447.08) * mm});
            skLineSegment(sketch, "E333", {"start": v(-8421.67, 6887.92) * mm, "end": v(-7303.33, 6887.92) * mm});
            skLineSegment(sketch, "E334", {"start": v(-7303.33, 6887.92) * mm, "end": v(-7303.33, 7015) * mm});
            skLineSegment(sketch, "E335", {"start": v(-8421.67, 7015) * mm, "end": v(-7303.33, 7015) * mm});
            skLineSegment(sketch, "E336", {"start": v(-5829.17, 5972.92) * mm, "end": v(-5371.67, 5972.92) * mm});
            skLineSegment(sketch, "E337", {"start": v(-8421.67, 5972.92) * mm, "end": v(-5956.25, 5972.92) * mm});
            skLineSegment(sketch, "E338", {"start": v(-8421.67, 4625.83) * mm, "end": v(-8421.67, 5845.83) * mm});
            skLineSegment(sketch, "E339", {"start": v(-8421.67, 101.67) * mm, "end": v(-8421.67, 1321.67) * mm});
            skLineSegment(sketch, "E340", {"start": v(-6439.17, -2160.42) * mm, "end": v(-5956.25, -2160.42) * mm});
            skLineSegment(sketch, "E341", {"start": v(-6439.17, -2160.42) * mm, "end": v(-6439.17, -2033.33) * mm});
            skLineSegment(sketch, "E342", {"start": v(-6439.17, 2490.83) * mm, "end": v(-5829.17, 2490.83) * mm});
            skLineSegment(sketch, "E343", {"start": v(-6439.17, 2363.75) * mm, "end": v(-5956.25, 2363.75) * mm});
            skLineSegment(sketch, "E344", {"start": v(-6439.17, 2363.75) * mm, "end": v(-6439.17, 2490.83) * mm});
            skLineSegment(sketch, "E345", {"start": v(-5829.17, 2490.83) * mm, "end": v(-5829.17, 1448.75) * mm});
            skLineSegment(sketch, "E346", {"start": v(-5956.25, 1448.75) * mm, "end": v(-5956.25, 2363.75) * mm});
            skLineSegment(sketch, "E347", {"start": v(-6439.17, 7015) * mm, "end": v(-5829.17, 7015) * mm});
            skLineSegment(sketch, "E348", {"start": v(-6439.17, 6887.92) * mm, "end": v(-5956.25, 6887.92) * mm});
            skLineSegment(sketch, "E349", {"start": v(-6439.17, 6887.92) * mm, "end": v(-6439.17, 7015) * mm});
            skLineSegment(sketch, "E350", {"start": v(-5829.17, 7015) * mm, "end": v(-5829.17, 5972.92) * mm});
            skLineSegment(sketch, "E351", {"start": v(-5956.25, 5972.92) * mm, "end": v(-5956.25, 6887.92) * mm});
            skLineSegment(sketch, "E352", {"start": v(-2830, -2160.42) * mm, "end": v(-3312.92, -2160.42) * mm});
            skLineSegment(sketch, "E353", {"start": v(-2830, -2160.42) * mm, "end": v(-2830, -2033.33) * mm});
            skLineSegment(sketch, "E354", {"start": v(-2830, 2490.83) * mm, "end": v(-3440, 2490.83) * mm});
            skLineSegment(sketch, "E355", {"start": v(-2830, 2363.75) * mm, "end": v(-3312.92, 2363.75) * mm});
            skLineSegment(sketch, "E356", {"start": v(-2830, 2363.75) * mm, "end": v(-2830, 2490.83) * mm});
            skLineSegment(sketch, "E357", {"start": v(-3440, 2490.83) * mm, "end": v(-3440, 1448.75) * mm});
            skLineSegment(sketch, "E358", {"start": v(-3312.92, 1448.75) * mm, "end": v(-3312.92, 2363.75) * mm});
            skLineSegment(sketch, "E359", {"start": v(-2830, 7015) * mm, "end": v(-3440, 7015) * mm});
            skLineSegment(sketch, "E360", {"start": v(-2830, 6887.92) * mm, "end": v(-3312.92, 6887.92) * mm});
            skLineSegment(sketch, "E361", {"start": v(-2830, 6887.92) * mm, "end": v(-2830, 7015) * mm});
            skLineSegment(sketch, "E362", {"start": v(-3440, 7015) * mm, "end": v(-3440, 5972.92) * mm});
            skLineSegment(sketch, "E363", {"start": v(-3312.92, 5972.92) * mm, "end": v(-3312.92, 6887.92) * mm});
            skLineSegment(sketch, "E364", {"start": v(-8421.67, -5998.3) * mm, "end": v(-5244.58, -5998.3) * mm});
            skLineSegment(sketch, "E365", {"start": v(-8421.67, -5871.22) * mm, "end": v(-5371.67, -5871.22) * mm});
            skLineSegment(sketch, "E366", {"start": v(-5371.67, -5871.22) * mm, "end": v(-5371.67, -4244.58) * mm});
            skLineSegment(sketch, "E367", {"start": v(-8421.67, -5871.22) * mm, "end": v(-8421.67, -4913.86) * mm});
            skLineSegment(sketch, "E368", {"start": v(-5244.58, -4549.58) * mm, "end": v(-5244.58, -5998.3) * mm});
            skLineSegment(sketch, "E369", {"start": v(-790.31, -10268.33) * mm, "end": v(-790.31, -10471.67) * mm});
            skLineSegment(sketch, "E370", {"start": v(-1705.31, -10268.33) * mm, "end": v(-1705.31, -10471.67) * mm});
            skLineSegment(sketch, "E371", {"start": v(-1705.31, -10471.67) * mm, "end": v(-4973.46, -10471.67) * mm});
            skLineSegment(sketch, "E372", {"start": v(-1705.31, -10268.33) * mm, "end": v(-2918.96, -10268.33) * mm});
            skLineSegment(sketch, "E373", {"start": v(-847.5, -8209.58) * mm, "end": v(-1749.8, -8209.58) * mm});
            skLineSegment(sketch, "E374", {"start": v(-2918.96, -8336.67) * mm, "end": v(-2918.96, -10268.33) * mm});
            skLineSegment(sketch, "E375", {"start": v(-1749.8, -8209.58) * mm, "end": v(-1749.8, -8336.67) * mm});
            skLineSegment(sketch, "E376", {"start": v(-2613.96, -8336.67) * mm, "end": v(-2613.96, -8209.58) * mm});
            skLineSegment(sketch, "E377", {"start": v(-2613.96, -8209.58) * mm, "end": v(-2918.96, -8209.58) * mm});
            skLineSegment(sketch, "E378", {"start": v(-2613.96, -8336.67) * mm, "end": v(-2918.96, -8336.67) * mm});
            skLineSegment(sketch, "E379", {"start": v(6625, -2652.81) * mm, "end": v(8625, -2652.81) * mm, "construction": true});
            skLineSegment(sketch, "E380", {"start": v(6625, -4652.81) * mm, "end": v(8625, -4652.81) * mm, "construction": true});
            skLineSegment(sketch, "E381", {"start": v(8625, -2652.81) * mm, "end": v(8625, -9217.81) * mm, "construction": true});
            skLineSegment(sketch, "E382", {"start": v(6625, -4957.81) * mm, "end": v(8625, -4957.81) * mm, "construction": true});
            skLineSegment(sketch, "E383", {"start": v(6625, -5262.81) * mm, "end": v(8625, -5262.81) * mm, "construction": true});
            skLineSegment(sketch, "E384", {"start": v(6625, -5567.81) * mm, "end": v(8625, -5567.81) * mm, "construction": true});
            skLineSegment(sketch, "E385", {"start": v(6625, -6177.81) * mm, "end": v(8625, -6177.81) * mm, "construction": true});
            skLineSegment(sketch, "E386", {"start": v(6625, -6482.81) * mm, "end": v(8625, -6482.81) * mm, "construction": true});
            skLineSegment(sketch, "E387", {"start": v(6625, -5872.81) * mm, "end": v(8625, -5872.81) * mm, "construction": true});
            skLineSegment(sketch, "E388", {"start": v(6625, -7092.81) * mm, "end": v(8625, -7092.81) * mm, "construction": true});
            skLineSegment(sketch, "E389", {"start": v(6625, -7397.81) * mm, "end": v(8625, -7397.81) * mm, "construction": true});
            skLineSegment(sketch, "E390", {"start": v(6625, -6787.81) * mm, "end": v(8625, -6787.81) * mm, "construction": true});
            skLineSegment(sketch, "E391", {"start": v(6625, -8007.81) * mm, "end": v(8625, -8007.81) * mm, "construction": true});
            skLineSegment(sketch, "E392", {"start": v(6625, -8312.81) * mm, "end": v(8625, -8312.81) * mm, "construction": true});
            skLineSegment(sketch, "E393", {"start": v(6625, -7702.81) * mm, "end": v(8625, -7702.81) * mm, "construction": true});
            skLineSegment(sketch, "E394", {"start": v(6625, -8912.81) * mm, "end": v(8625, -8912.81) * mm, "construction": true});
            skLineSegment(sketch, "E395", {"start": v(6625, -9217.81) * mm, "end": v(8625, -9217.81) * mm, "construction": true});
            skLineSegment(sketch, "E396", {"start": v(6625, -8607.81) * mm, "end": v(8625, -8607.81) * mm, "construction": true});
            skLineSegment(sketch, "E397", {"start": v(7575, -9222.81) * mm, "end": v(7575, -5012.81) * mm, "construction": true});
            skLineSegment(sketch, "E398", {"start": v(7575, -5012.81) * mm, "end": v(7667.75, -5144.63) * mm, "construction": true});
            skLineSegment(sketch, "E399", {"start": v(7575, -5012.81) * mm, "end": v(7498.6, -5139.34) * mm, "construction": true});
            skLineSegment(sketch, "E400", {"start": v(6421.67, 2795.83) * mm, "end": v(6625, 2795.83) * mm});
            skLineSegment(sketch, "E401", {"start": v(6421.67, 1880.83) * mm, "end": v(6625, 1880.83) * mm});
            skLineSegment(sketch, "E402.trimOffspring", {"start": v(-720.42, -2033.33) * mm, "end": v(-377.3, -2033.33) * mm});
            skLineSegment(sketch, "E403.trimOffspring", {"start": v(1351.04, -2173.12) * mm, "end": v(1919.8, -2173.12) * mm});
            skSolve(sketch);
        }
        {
            var Q0;
            Q0 = qSketchRegion(id + "F0", true);
            extrude(context, id + "F1", {"entities" : qUnion([Q0]), "depth" : 3400 * mm, "offsetDistance" : 25 * mm});
        }
        {
            var Q0;
            Q0=makeQuery(id+"F1.opExtrude","CAP_FACE",FACE,{"disambiguationData":[OSD([sQuery(id+"F0.wireOp",EDGE,"E1"),sQuery(id+"F0.wireOp",EDGE,"E25"),sQuery(id+"F0.wireOp",EDGE,"E26"),sQuery(id+"F0.wireOp",EDGE,"E27"),sQuery(id+"F0.wireOp",EDGE,"E47"),sQuery(id+"F0.wireOp",EDGE,"E120"),sQuery(id+"F0.wireOp",EDGE,"E121"),sQuery(id+"F0.wireOp",EDGE,"E122"),sQuery(id+"F0.wireOp",EDGE,"E123"),sQuery(id+"F0.wireOp",EDGE,"E124"),sQuery(id+"F0.wireOp",EDGE,"E125"),sQuery(id+"F0.wireOp",EDGE,"E126"),sQuery(id+"F0.wireOp",EDGE,"E131"),sQuery(id+"F0.wireOp",EDGE,"c3e2b968-5de1-4c9e-a235-90de6999c33d"),sQuery(id+"F0.wireOp",EDGE,"E132"),sQuery(id+"F0.wireOp",EDGE,"E133"),sQuery(id+"F0.wireOp",EDGE,"E139"),sQuery(id+"F0.wireOp",EDGE,"E174"),sQuery(id+"F0.wireOp",EDGE,"E175"),sQuery(id+"F0.wireOp",EDGE,"E176"),sQuery(id+"F0.wireOp",EDGE,"E177"),sQuery(id+"F0.wireOp",EDGE,"E178"),sQuery(id+"F0.wireOp",EDGE,"E179"),sQuery(id+"F0.wireOp",EDGE,"E180"),sQuery(id+"F0.wireOp",EDGE,"E182"),sQuery(id+"F0.wireOp",EDGE,"E183"),sQuery(id+"F0.wireOp",EDGE,"E184"),sQuery(id+"F0.wireOp",EDGE,"E185"),sQuery(id+"F0.wireOp",EDGE,"E186"),sQuery(id+"F0.wireOp",EDGE,"E187"),sQuery(id+"F0.wireOp",EDGE,"E188"),sQuery(id+"F0.wireOp",EDGE,"E189"),sQuery(id+"F0.wireOp",EDGE,"E190"),sQuery(id+"F0.wireOp",EDGE,"E191"),sQuery(id+"F0.wireOp",EDGE,"E192"),sQuery(id+"F0.wireOp",EDGE,"E193"),sQuery(id+"F0.wireOp",EDGE,"E206"),sQuery(id+"F0.wireOp",EDGE,"E207"),sQuery(id+"F0.wireOp",EDGE,"E208"),sQuery(id+"F0.wireOp",EDGE,"E209"),sQuery(id+"F0.wireOp",EDGE,"E210"),sQuery(id+"F0.wireOp",EDGE,"E211"),sQuery(id+"F0.wireOp",EDGE,"E212"),sQuery(id+"F0.wireOp",EDGE,"E213"),sQuery(id+"F0.wireOp",EDGE,"E243"),sQuery(id+"F0.wireOp",EDGE,"E256"),sQuery(id+"F0.wireOp",EDGE,"E268"),sQuery(id+"F0.wireOp",EDGE,"E269"),sQuery(id+"F0.wireOp",EDGE,"E277"),sQuery(id+"F0.wireOp",EDGE,"E278"),sQuery(id+"F0.wireOp",EDGE,"E279"),sQuery(id+"F0.wireOp",EDGE,"E281"),sQuery(id+"F0.wireOp",EDGE,"E282"),sQuery(id+"F0.wireOp",EDGE,"E283"),sQuery(id+"F0.wireOp",EDGE,"E284"),sQuery(id+"F0.wireOp",EDGE,"E285"),sQuery(id+"F0.wireOp",EDGE,"E286"),sQuery(id+"F0.wireOp",EDGE,"E287"),sQuery(id+"F0.wireOp",EDGE,"E288"),sQuery(id+"F0.wireOp",EDGE,"E290"),sQuery(id+"F0.wireOp",EDGE,"E291"),sQuery(id+"F0.wireOp",EDGE,"E292"),sQuery(id+"F0.wireOp",EDGE,"E293"),sQuery(id+"F0.wireOp",EDGE,"E294"),sQuery(id+"F0.wireOp",EDGE,"E295"),sQuery(id+"F0.wireOp",EDGE,"E296"),sQuery(id+"F0.wireOp",EDGE,"E352"),sQuery(id+"F0.wireOp",EDGE,"E353"),sQuery(id+"F0.wireOp",EDGE,"E354"),sQuery(id+"F0.wireOp",EDGE,"E355"),sQuery(id+"F0.wireOp",EDGE,"E356"),sQuery(id+"F0.wireOp",EDGE,"E357"),sQuery(id+"F0.wireOp",EDGE,"E358"),sQuery(id+"F0.wireOp",EDGE,"E359"),sQuery(id+"F0.wireOp",EDGE,"E360"),sQuery(id+"F0.wireOp",EDGE,"E361"),sQuery(id+"F0.wireOp",EDGE,"E362"),sQuery(id+"F0.wireOp",EDGE,"E363")])],"isStart":true});
            var sketch = newSketch(context, id + "F2", { "sketchPlane" : qUnion([Q0])});
            skLineSegment(sketch, "E404.bottom", {"start": v(-8625, 10471.67) * mm, "end": v(440.07, 10471.67) * mm});
            skLineSegment(sketch, "E404.top", {"start": v(-8625, -11488.33) * mm, "end": v(6625, -11488.33) * mm});
            skLineSegment(sketch, "E404.left", {"start": v(-8625, 10471.67) * mm, "end": v(-8625, -11488.33) * mm});
            skLineSegment(sketch, "E404.right", {"start": v(6625, 10471.67) * mm, "end": v(6625, -11488.33) * mm});
            skLineSegment(sketch, "E405.0", {"start": v(440.07, 10471.67) * mm, "end": v(1100.9, 11488.33) * mm});
            skLineSegment(sketch, "E405.1", {"start": v(2744.93, 11488.33) * mm, "end": v(1100.9, 11488.33) * mm});
            skLineSegment(sketch, "E405.2", {"start": v(3405.76, 10471.67) * mm, "end": v(2744.93, 11488.33) * mm});
            skLineSegment(sketch, "E406.trimOffspring", {"start": v(3405.76, 10471.67) * mm, "end": v(6625, 10471.67) * mm});
            skSolve(sketch);
        }
        {
            var Q0;
            Q0 = qSketchRegion(id + "F2", true);
            extrude(context, id + "F3", {"entities" : qUnion([Q0]), "operationType" : NewBodyOperationType.ADD, "depth" : 300 * mm, "offsetDistance" : 25 * mm});
        }
        {
            var Q0;
            Q0=makeQuery(id+"F3.opExtrude","CAP_FACE",FACE,{"disambiguationData":[OSD([sQuery(id+"F2.wireOp",EDGE,"E404.bottom"),sQuery(id+"F2.wireOp",EDGE,"E404.top"),sQuery(id+"F2.wireOp",EDGE,"E404.left"),sQuery(id+"F2.wireOp",EDGE,"E404.right"),sQuery(id+"F2.wireOp",EDGE,"E405.0"),sQuery(id+"F2.wireOp",EDGE,"E405.1"),sQuery(id+"F2.wireOp",EDGE,"E405.2"),sQuery(id+"F2.wireOp",EDGE,"E406.trimOffspring")])],"isStart":true});
            var sketch = newSketch(context, id + "F4", { "sketchPlane" : qUnion([Q0])});
            skLineSegment(sketch, "E407.bottom", {"start": v(-5888.46, -10268.33) * mm, "end": v(-4973.46, -10268.33) * mm});
            skLineSegment(sketch, "E407.top", {"start": v(-5888.46, -10471.67) * mm, "end": v(-4973.46, -10471.67) * mm});
            skLineSegment(sketch, "E407.left", {"start": v(-5888.46, -10268.33) * mm, "end": v(-5888.46, -10471.67) * mm});
            skLineSegment(sketch, "E407.right", {"start": v(-4973.46, -10268.33) * mm, "end": v(-4973.46, -10471.67) * mm});
            skLineSegment(sketch, "E408.bottom", {"start": v(-1705.31, -10268.33) * mm, "end": v(-790.31, -10268.33) * mm});
            skLineSegment(sketch, "E408.top", {"start": v(-1705.31, -10471.67) * mm, "end": v(-790.31, -10471.67) * mm});
            skLineSegment(sketch, "E408.left", {"start": v(-1705.31, -10268.33) * mm, "end": v(-1705.31, -10471.67) * mm});
            skLineSegment(sketch, "E408.right", {"start": v(-790.31, -10268.33) * mm, "end": v(-790.31, -10471.67) * mm});
            skLineSegment(sketch, "E409.bottom", {"start": v(-8625, -6955.68) * mm, "end": v(-8421.67, -6955.68) * mm});
            skLineSegment(sketch, "E409.top", {"start": v(-8625, -7870.68) * mm, "end": v(-8421.67, -7870.68) * mm});
            skLineSegment(sketch, "E409.left", {"start": v(-8625, -6955.68) * mm, "end": v(-8625, -7870.68) * mm});
            skLineSegment(sketch, "E409.right", {"start": v(-8421.67, -6955.68) * mm, "end": v(-8421.67, -7870.68) * mm});
            skLineSegment(sketch, "E410.bottom", {"start": v(-8625, -3998.86) * mm, "end": v(-8421.67, -3998.86) * mm});
            skLineSegment(sketch, "E410.top", {"start": v(-8625, -4913.86) * mm, "end": v(-8421.67, -4913.86) * mm});
            skLineSegment(sketch, "E410.left", {"start": v(-8625, -3998.86) * mm, "end": v(-8625, -4913.86) * mm});
            skLineSegment(sketch, "E410.right", {"start": v(-8421.67, -3998.86) * mm, "end": v(-8421.67, -4913.86) * mm});
            skLineSegment(sketch, "E411.bottom", {"start": v(-8625, 101.67) * mm, "end": v(-8421.67, 101.67) * mm});
            skLineSegment(sketch, "E411.top", {"start": v(-8625, -813.33) * mm, "end": v(-8421.67, -813.33) * mm});
            skLineSegment(sketch, "E411.left", {"start": v(-8625, 101.67) * mm, "end": v(-8625, -813.33) * mm});
            skLineSegment(sketch, "E411.right", {"start": v(-8421.67, 101.67) * mm, "end": v(-8421.67, -813.33) * mm});
            skLineSegment(sketch, "E412.bottom", {"start": v(-8625, 4625.83) * mm, "end": v(-8421.67, 4625.83) * mm});
            skLineSegment(sketch, "E412.top", {"start": v(-8625, 3710.83) * mm, "end": v(-8421.67, 3710.83) * mm});
            skLineSegment(sketch, "E412.left", {"start": v(-8625, 4625.83) * mm, "end": v(-8625, 3710.83) * mm});
            skLineSegment(sketch, "E412.right", {"start": v(-8421.67, 4625.83) * mm, "end": v(-8421.67, 3710.83) * mm});
            skLineSegment(sketch, "E413.bottom", {"start": v(-8625, 8997.5) * mm, "end": v(-8421.67, 8997.5) * mm});
            skLineSegment(sketch, "E413.top", {"start": v(-8625, 8082.5) * mm, "end": v(-8421.67, 8082.5) * mm});
            skLineSegment(sketch, "E413.left", {"start": v(-8625, 8997.5) * mm, "end": v(-8625, 8082.5) * mm});
            skLineSegment(sketch, "E413.right", {"start": v(-8421.67, 8997.5) * mm, "end": v(-8421.67, 8082.5) * mm});
            skLineSegment(sketch, "E414.bottom", {"start": v(-949.17, 11488.33) * mm, "end": v(-34.17, 11488.33) * mm});
            skLineSegment(sketch, "E414.top", {"start": v(-949.17, 11285) * mm, "end": v(-34.17, 11285) * mm});
            skLineSegment(sketch, "E414.left", {"start": v(-949.17, 11488.33) * mm, "end": v(-949.17, 11285) * mm});
            skLineSegment(sketch, "E414.right", {"start": v(-34.17, 11488.33) * mm, "end": v(-34.17, 11285) * mm});
            skLineSegment(sketch, "E415.bottom", {"start": v(4070.62, 11488.33) * mm, "end": v(4985.62, 11488.33) * mm});
            skLineSegment(sketch, "E415.top", {"start": v(4070.62, 11285) * mm, "end": v(4985.62, 11285) * mm});
            skLineSegment(sketch, "E415.left", {"start": v(4070.62, 11488.33) * mm, "end": v(4070.62, 11285) * mm});
            skLineSegment(sketch, "E415.right", {"start": v(4985.62, 11488.33) * mm, "end": v(4985.62, 11285) * mm});
            skLineSegment(sketch, "E416.bottom", {"start": v(6421.67, 5731.46) * mm, "end": v(6625, 5731.46) * mm});
            skLineSegment(sketch, "E416.top", {"start": v(6421.67, 4816.46) * mm, "end": v(6625, 4816.46) * mm});
            skLineSegment(sketch, "E416.left", {"start": v(6421.67, 5731.46) * mm, "end": v(6421.67, 4816.46) * mm});
            skLineSegment(sketch, "E416.right", {"start": v(6625, 5731.46) * mm, "end": v(6625, 4816.46) * mm});
            skLineSegment(sketch, "E417.bottom", {"start": v(6421.67, 2795.83) * mm, "end": v(6625, 2795.83) * mm});
            skLineSegment(sketch, "E417.top", {"start": v(6421.67, 1880.83) * mm, "end": v(6625, 1880.83) * mm});
            skLineSegment(sketch, "E417.left", {"start": v(6421.67, 2795.83) * mm, "end": v(6421.67, 1880.83) * mm});
            skLineSegment(sketch, "E417.right", {"start": v(6625, 2795.83) * mm, "end": v(6625, 1880.83) * mm});
            skSolve(sketch);
        }
        {
            var Q0;
            Q0 = qSketchRegion(id + "F4", true);
            extrude(context, id + "F5", {"entities" : qUnion([Q0]), "operationType" : NewBodyOperationType.ADD, "depth" : 1850 * mm, "offsetDistance" : 25 * mm});
        }
        {
            var Q0;
            Q0=makeQuery(id+"F1.opExtrude","CAP_FACE",FACE,{"disambiguationData":[OSD([sQuery(id+"F0.wireOp",EDGE,"E32"),sQuery(id+"F0.wireOp",EDGE,"E33"),sQuery(id+"F0.wireOp",EDGE,"E34"),sQuery(id+"F0.wireOp",EDGE,"E35"),sQuery(id+"F0.wireOp",EDGE,"E36"),sQuery(id+"F0.wireOp",EDGE,"E37"),sQuery(id+"F0.wireOp",EDGE,"E38"),sQuery(id+"F0.wireOp",EDGE,"E39"),sQuery(id+"F0.wireOp",EDGE,"E40"),sQuery(id+"F0.wireOp",EDGE,"E41"),sQuery(id+"F0.wireOp",EDGE,"E42"),sQuery(id+"F0.wireOp",EDGE,"E43"),sQuery(id+"F0.wireOp",EDGE,"E44"),sQuery(id+"F0.wireOp",EDGE,"E45"),sQuery(id+"F0.wireOp",EDGE,"E69"),sQuery(id+"F0.wireOp",EDGE,"E70"),sQuery(id+"F0.wireOp",EDGE,"E98"),sQuery(id+"F0.wireOp",EDGE,"E99"),sQuery(id+"F0.wireOp",EDGE,"E100"),sQuery(id+"F0.wireOp",EDGE,"E101"),sQuery(id+"F0.wireOp",EDGE,"E102"),sQuery(id+"F0.wireOp",EDGE,"E103"),sQuery(id+"F0.wireOp",EDGE,"E104"),sQuery(id+"F0.wireOp",EDGE,"E105"),sQuery(id+"F0.wireOp",EDGE,"E194"),sQuery(id+"F0.wireOp",EDGE,"E205"),sQuery(id+"F0.wireOp",EDGE,"E254"),sQuery(id+"F0.wireOp",EDGE,"E257"),sQuery(id+"F0.wireOp",EDGE,"E46"),sQuery(id+"F0.wireOp",EDGE,"E270")])],"isStart":false});
            var sketch = newSketch(context, id + "F6", { "sketchPlane" : qUnion([Q0])});
            skLineSegment(sketch, "E418.0", {"start": v(-949.17, 11285) * mm, "end": v(-949.17, 11488.33) * mm});
            skLineSegment(sketch, "E418.1", {"start": v(-34.17, 11285) * mm, "end": v(-34.17, 11488.33) * mm});
            skLineSegment(sketch, "E419", {"start": v(-949.17, 11488.33) * mm, "end": v(-34.17, 11488.33) * mm});
            skLineSegment(sketch, "E420", {"start": v(-34.17, 11285) * mm, "end": v(-949.17, 11285) * mm});
            skLineSegment(sketch, "E421.0", {"start": v(4070.62, 11285) * mm, "end": v(4070.62, 11488.33) * mm});
            skLineSegment(sketch, "E421.1", {"start": v(4985.62, 11285) * mm, "end": v(4985.62, 11488.33) * mm});
            skLineSegment(sketch, "E422", {"start": v(4070.62, 11488.33) * mm, "end": v(4985.62, 11488.33) * mm});
            skLineSegment(sketch, "E423", {"start": v(4985.62, 11285) * mm, "end": v(4070.62, 11285) * mm});
            skLineSegment(sketch, "E424.0", {"start": v(-790.31, -10268.33) * mm, "end": v(-790.31, -10471.67) * mm});
            skLineSegment(sketch, "E424.1", {"start": v(-1705.31, -10268.33) * mm, "end": v(-1705.31, -10471.67) * mm});
            skLineSegment(sketch, "E424.2", {"start": v(-5888.46, -10471.67) * mm, "end": v(-5888.46, -10268.33) * mm});
            skLineSegment(sketch, "E424.3", {"start": v(-4973.46, -10471.67) * mm, "end": v(-4973.46, -10268.33) * mm});
            skLineSegment(sketch, "E425", {"start": v(-5888.46, -10268.33) * mm, "end": v(-4973.46, -10268.33) * mm});
            skLineSegment(sketch, "E426", {"start": v(-5888.46, -10471.67) * mm, "end": v(-4973.46, -10471.67) * mm});
            skLineSegment(sketch, "E427", {"start": v(-1705.31, -10471.67) * mm, "end": v(-790.31, -10471.67) * mm});
            skLineSegment(sketch, "E428", {"start": v(-790.31, -10268.33) * mm, "end": v(-1705.31, -10268.33) * mm});
            skLineSegment(sketch, "E429.0", {"start": v(-8421.67, -6955.68) * mm, "end": v(-8625, -6955.68) * mm});
            skLineSegment(sketch, "E429.1", {"start": v(-8421.67, -7870.68) * mm, "end": v(-8625, -7870.68) * mm});
            skLineSegment(sketch, "E430", {"start": v(-8625, -6955.68) * mm, "end": v(-8625, -7870.68) * mm});
            skLineSegment(sketch, "E431", {"start": v(-8421.67, -6955.68) * mm, "end": v(-8421.67, -7870.68) * mm});
            skLineSegment(sketch, "E432.0", {"start": v(-8421.67, -3998.86) * mm, "end": v(-8625, -3998.86) * mm});
            skLineSegment(sketch, "E432.1", {"start": v(-8421.67, -4913.86) * mm, "end": v(-8625, -4913.86) * mm});
            skLineSegment(sketch, "E432.2", {"start": v(-8421.67, 101.67) * mm, "end": v(-8625, 101.67) * mm});
            skLineSegment(sketch, "E432.3", {"start": v(-8421.67, -813.33) * mm, "end": v(-8625, -813.33) * mm});
            skLineSegment(sketch, "E432.4", {"start": v(-8421.67, 4625.83) * mm, "end": v(-8625, 4625.83) * mm});
            skLineSegment(sketch, "E432.5", {"start": v(-8421.67, 3710.83) * mm, "end": v(-8625, 3710.83) * mm});
            skLineSegment(sketch, "E432.6", {"start": v(-8421.67, 8997.5) * mm, "end": v(-8625, 8997.5) * mm});
            skLineSegment(sketch, "E432.7", {"start": v(-8421.67, 8082.5) * mm, "end": v(-8625, 8082.5) * mm});
            skLineSegment(sketch, "E433", {"start": v(-8625, 8997.5) * mm, "end": v(-8625, 8082.5) * mm});
            skLineSegment(sketch, "E434.trimOffspring", {"start": v(-8625, 4625.83) * mm, "end": v(-8625, 3710.83) * mm});
            skLineSegment(sketch, "E435.trimOffspring", {"start": v(-8421.67, 8082.5) * mm, "end": v(-8421.67, 8997.5) * mm});
            skLineSegment(sketch, "E436.trimOffspring", {"start": v(-8421.67, 3710.83) * mm, "end": v(-8421.67, 4625.83) * mm});
            skLineSegment(sketch, "E437.trimOffspring", {"start": v(-8421.67, -813.33) * mm, "end": v(-8421.67, 101.67) * mm});
            skLineSegment(sketch, "E438.trimOffspring", {"start": v(-8421.67, -4913.86) * mm, "end": v(-8421.67, -3998.86) * mm});
            skLineSegment(sketch, "E439.trimOffspring", {"start": v(-8625, -3998.86) * mm, "end": v(-8625, -4913.86) * mm});
            skLineSegment(sketch, "E440.2", {"start": v(6421.67, 1880.83) * mm, "end": v(6625, 1880.83) * mm});
            skLineSegment(sketch, "E440.3", {"start": v(6421.67, 2795.83) * mm, "end": v(6625, 2795.83) * mm});
            skLineSegment(sketch, "E440.4", {"start": v(6421.67, 5731.46) * mm, "end": v(6625, 5731.46) * mm});
            skLineSegment(sketch, "E440.5", {"start": v(6421.67, 4816.46) * mm, "end": v(6625, 4816.46) * mm});
            skLineSegment(sketch, "E441", {"start": v(6421.67, 2795.83) * mm, "end": v(6421.67, 1880.83) * mm});
            skLineSegment(sketch, "E442", {"start": v(6625, 2795.83) * mm, "end": v(6625, 1880.83) * mm});
            skLineSegment(sketch, "E443", {"start": v(6421.67, 5731.46) * mm, "end": v(6421.67, 4816.46) * mm});
            skLineSegment(sketch, "E444", {"start": v(6625, 5731.46) * mm, "end": v(6625, 4816.46) * mm});
            skLineSegment(sketch, "E445", {"start": v(-8625, 101.67) * mm, "end": v(-8625, -813.33) * mm});
            skSolve(sketch);
        }
        {
            var Q0;
            Q0 = qSketchRegion(id + "F6", true);
            extrude(context, id + "F7", {"entities" : qUnion([Q0]), "operationType" : NewBodyOperationType.ADD, "oppositeDirection" : true, "depth" : 100 * mm, "offsetDistance" : 25 * mm});
        }
        {
            var Q0;
            Q0=makeQuery(id+"F7.boolean.opBoolean","MERGE",FACE,{"derivedFrom":[makeQuery(id+"F1.opExtrude","CAP_FACE",FACE,{"disambiguationData":[OSD([sQuery(id+"F0.wireOp",EDGE,"E0"),sQuery(id+"F0.wireOp",EDGE,"E4"),sQuery(id+"F0.wireOp",EDGE,"E248"),sQuery(id+"F0.wireOp",EDGE,"E250"),sQuery(id+"F0.wireOp",EDGE,"E258"),sQuery(id+"F0.wireOp",EDGE,"E259")])],"isStart":false}),makeQuery(id+"F1.opExtrude","CAP_FACE",FACE,{"disambiguationData":[OSD([sQuery(id+"F0.wireOp",EDGE,"E1"),sQuery(id+"F0.wireOp",EDGE,"E25"),sQuery(id+"F0.wireOp",EDGE,"E26"),sQuery(id+"F0.wireOp",EDGE,"E27"),sQuery(id+"F0.wireOp",EDGE,"E47"),sQuery(id+"F0.wireOp",EDGE,"E120"),sQuery(id+"F0.wireOp",EDGE,"E121"),sQuery(id+"F0.wireOp",EDGE,"E122"),sQuery(id+"F0.wireOp",EDGE,"E123"),sQuery(id+"F0.wireOp",EDGE,"E124"),sQuery(id+"F0.wireOp",EDGE,"E125"),sQuery(id+"F0.wireOp",EDGE,"E126"),sQuery(id+"F0.wireOp",EDGE,"E131"),sQuery(id+"F0.wireOp",EDGE,"c3e2b968-5de1-4c9e-a235-90de6999c33d"),sQuery(id+"F0.wireOp",EDGE,"E132"),sQuery(id+"F0.wireOp",EDGE,"E133"),sQuery(id+"F0.wireOp",EDGE,"E139"),sQuery(id+"F0.wireOp",EDGE,"E174"),sQuery(id+"F0.wireOp",EDGE,"E175"),sQuery(id+"F0.wireOp",EDGE,"E176"),sQuery(id+"F0.wireOp",EDGE,"E177"),sQuery(id+"F0.wireOp",EDGE,"E178"),sQuery(id+"F0.wireOp",EDGE,"E179"),sQuery(id+"F0.wireOp",EDGE,"E180"),sQuery(id+"F0.wireOp",EDGE,"E182"),sQuery(id+"F0.wireOp",EDGE,"E183"),sQuery(id+"F0.wireOp",EDGE,"E184"),sQuery(id+"F0.wireOp",EDGE,"E185"),sQuery(id+"F0.wireOp",EDGE,"E186"),sQuery(id+"F0.wireOp",EDGE,"E187"),sQuery(id+"F0.wireOp",EDGE,"E188"),sQuery(id+"F0.wireOp",EDGE,"E189"),sQuery(id+"F0.wireOp",EDGE,"E190"),sQuery(id+"F0.wireOp",EDGE,"E191"),sQuery(id+"F0.wireOp",EDGE,"E192"),sQuery(id+"F0.wireOp",EDGE,"E193"),sQuery(id+"F0.wireOp",EDGE,"E206"),sQuery(id+"F0.wireOp",EDGE,"E207"),sQuery(id+"F0.wireOp",EDGE,"E208"),sQuery(id+"F0.wireOp",EDGE,"E209"),sQuery(id+"F0.wireOp",EDGE,"E210"),sQuery(id+"F0.wireOp",EDGE,"E211"),sQuery(id+"F0.wireOp",EDGE,"E212"),sQuery(id+"F0.wireOp",EDGE,"E213"),sQuery(id+"F0.wireOp",EDGE,"E243"),sQuery(id+"F0.wireOp",EDGE,"E256"),sQuery(id+"F0.wireOp",EDGE,"E268"),sQuery(id+"F0.wireOp",EDGE,"E269"),sQuery(id+"F0.wireOp",EDGE,"E277"),sQuery(id+"F0.wireOp",EDGE,"E278"),sQuery(id+"F0.wireOp",EDGE,"E279"),sQuery(id+"F0.wireOp",EDGE,"E281"),sQuery(id+"F0.wireOp",EDGE,"E282"),sQuery(id+"F0.wireOp",EDGE,"E283"),sQuery(id+"F0.wireOp",EDGE,"E284"),sQuery(id+"F0.wireOp",EDGE,"E285"),sQuery(id+"F0.wireOp",EDGE,"E286"),sQuery(id+"F0.wireOp",EDGE,"E287"),sQuery(id+"F0.wireOp",EDGE,"E288"),sQuery(id+"F0.wireOp",EDGE,"E290"),sQuery(id+"F0.wireOp",EDGE,"E291"),sQuery(id+"F0.wireOp",EDGE,"E292"),sQuery(id+"F0.wireOp",EDGE,"E293"),sQuery(id+"F0.wireOp",EDGE,"E294"),sQuery(id+"F0.wireOp",EDGE,"E295"),sQuery(id+"F0.wireOp",EDGE,"E296"),sQuery(id+"F0.wireOp",EDGE,"E352"),sQuery(id+"F0.wireOp",EDGE,"E353"),sQuery(id+"F0.wireOp",EDGE,"E354"),sQuery(id+"F0.wireOp",EDGE,"E355"),sQuery(id+"F0.wireOp",EDGE,"E356"),sQuery(id+"F0.wireOp",EDGE,"E357"),sQuery(id+"F0.wireOp",EDGE,"E358"),sQuery(id+"F0.wireOp",EDGE,"E359"),sQuery(id+"F0.wireOp",EDGE,"E360"),sQuery(id+"F0.wireOp",EDGE,"E361"),sQuery(id+"F0.wireOp",EDGE,"E362"),sQuery(id+"F0.wireOp",EDGE,"E363")])],"isStart":false}),makeQuery(id+"F1.opExtrude","CAP_FACE",FACE,{"disambiguationData":[OSD([sQuery(id+"F0.wireOp",EDGE,"E2"),sQuery(id+"F0.wireOp",EDGE,"E5"),sQuery(id+"F0.wireOp",EDGE,"E127"),sQuery(id+"F0.wireOp",EDGE,"E128"),sQuery(id+"F0.wireOp",EDGE,"E129"),sQuery(id+"F0.wireOp",EDGE,"E130"),sQuery(id+"F0.wireOp",EDGE,"E253"),sQuery(id+"F0.wireOp",EDGE,"E255"),sQuery(id+"F0.wireOp",EDGE,"E271"),sQuery(id+"F0.wireOp",EDGE,"E272")])],"isStart":false}),makeQuery(id+"F1.opExtrude","CAP_FACE",FACE,{"disambiguationData":[OSD([sQuery(id+"F0.wireOp",EDGE,"E3"),sQuery(id+"F0.wireOp",EDGE,"E6"),sQuery(id+"F0.wireOp",EDGE,"E7"),sQuery(id+"F0.wireOp",EDGE,"E8"),sQuery(id+"F0.wireOp",EDGE,"E9"),sQuery(id+"F0.wireOp",EDGE,"E10"),sQuery(id+"F0.wireOp",EDGE,"E11"),sQuery(id+"F0.wireOp",EDGE,"E13"),sQuery(id+"F0.wireOp",EDGE,"E14"),sQuery(id+"F0.wireOp",EDGE,"E16"),sQuery(id+"F0.wireOp",EDGE,"E17"),sQuery(id+"F0.wireOp",EDGE,"E18"),sQuery(id+"F0.wireOp",EDGE,"E19"),sQuery(id+"F0.wireOp",EDGE,"E20"),sQuery(id+"F0.wireOp",EDGE,"E24"),sQuery(id+"F0.wireOp",EDGE,"E28"),sQuery(id+"F0.wireOp",EDGE,"E30"),sQuery(id+"F0.wireOp",EDGE,"E31"),sQuery(id+"F0.wireOp",EDGE,"E64"),sQuery(id+"F0.wireOp",EDGE,"E65"),sQuery(id+"F0.wireOp",EDGE,"E66"),sQuery(id+"F0.wireOp",EDGE,"E67"),sQuery(id+"F0.wireOp",EDGE,"E75"),sQuery(id+"F0.wireOp",EDGE,"E97"),sQuery(id+"F0.wireOp",EDGE,"E116"),sQuery(id+"F0.wireOp",EDGE,"E135"),sQuery(id+"F0.wireOp",EDGE,"E136"),sQuery(id+"F0.wireOp",EDGE,"E137"),sQuery(id+"F0.wireOp",EDGE,"E156"),sQuery(id+"F0.wireOp",EDGE,"E157"),sQuery(id+"F0.wireOp",EDGE,"E158"),sQuery(id+"F0.wireOp",EDGE,"E159"),sQuery(id+"F0.wireOp",EDGE,"E160"),sQuery(id+"F0.wireOp",EDGE,"E161"),sQuery(id+"F0.wireOp",EDGE,"E162"),sQuery(id+"F0.wireOp",EDGE,"E163"),sQuery(id+"F0.wireOp",EDGE,"E195"),sQuery(id+"F0.wireOp",EDGE,"E196"),sQuery(id+"F0.wireOp",EDGE,"E235"),sQuery(id+"F0.wireOp",EDGE,"E238"),sQuery(id+"F0.wireOp",EDGE,"E241"),sQuery(id+"F0.wireOp",EDGE,"E369"),sQuery(id+"F0.wireOp",EDGE,"E373"),sQuery(id+"F0.wireOp",EDGE,"E375")])],"isStart":false}),makeQuery(id+"F1.opExtrude","CAP_FACE",FACE,{"disambiguationData":[OSD([sQuery(id+"F0.wireOp",EDGE,"E15"),sQuery(id+"F0.wireOp",EDGE,"E68"),sQuery(id+"F0.wireOp",EDGE,"E76"),sQuery(id+"F0.wireOp",EDGE,"E77"),sQuery(id+"F0.wireOp",EDGE,"E78"),sQuery(id+"F0.wireOp",EDGE,"E79"),sQuery(id+"F0.wireOp",EDGE,"E80"),sQuery(id+"F0.wireOp",EDGE,"E81"),sQuery(id+"F0.wireOp",EDGE,"E82"),sQuery(id+"F0.wireOp",EDGE,"E83"),sQuery(id+"F0.wireOp",EDGE,"E84"),sQuery(id+"F0.wireOp",EDGE,"E85"),sQuery(id+"F0.wireOp",EDGE,"E86"),sQuery(id+"F0.wireOp",EDGE,"E87"),sQuery(id+"F0.wireOp",EDGE,"E88"),sQuery(id+"F0.wireOp",EDGE,"E89"),sQuery(id+"F0.wireOp",EDGE,"E90"),sQuery(id+"F0.wireOp",EDGE,"E91"),sQuery(id+"F0.wireOp",EDGE,"E92"),sQuery(id+"F0.wireOp",EDGE,"E93"),sQuery(id+"F0.wireOp",EDGE,"E94"),sQuery(id+"F0.wireOp",EDGE,"E95"),sQuery(id+"F0.wireOp",EDGE,"E96"),sQuery(id+"F0.wireOp",EDGE,"E134"),sQuery(id+"F0.wireOp",EDGE,"E164"),sQuery(id+"F0.wireOp",EDGE,"E165"),sQuery(id+"F0.wireOp",EDGE,"E166"),sQuery(id+"F0.wireOp",EDGE,"E167"),sQuery(id+"F0.wireOp",EDGE,"E168"),sQuery(id+"F0.wireOp",EDGE,"E169"),sQuery(id+"F0.wireOp",EDGE,"E170"),sQuery(id+"F0.wireOp",EDGE,"99e792f0-c16b-4b1c-a76c-2567feb051d9"),sQuery(id+"F0.wireOp",EDGE,"E171"),sQuery(id+"F0.wireOp",EDGE,"E172"),sQuery(id+"F0.wireOp",EDGE,"E173"),sQuery(id+"F0.wireOp",EDGE,"E275"),sQuery(id+"F0.wireOp",EDGE,"E276"),sQuery(id+"F0.wireOp",EDGE,"E401")])],"isStart":false}),makeQuery(id+"F1.opExtrude","CAP_FACE",FACE,{"disambiguationData":[OSD([sQuery(id+"F0.wireOp",EDGE,"E21"),sQuery(id+"F0.wireOp",EDGE,"E22"),sQuery(id+"F0.wireOp",EDGE,"E23"),sQuery(id+"F0.wireOp",EDGE,"E71"),sQuery(id+"F0.wireOp",EDGE,"E72"),sQuery(id+"F0.wireOp",EDGE,"E73"),sQuery(id+"F0.wireOp",EDGE,"E74"),sQuery(id+"F0.wireOp",EDGE,"E113"),sQuery(id+"F0.wireOp",EDGE,"E251"),sQuery(id+"F0.wireOp",EDGE,"E370"),sQuery(id+"F0.wireOp",EDGE,"E371"),sQuery(id+"F0.wireOp",EDGE,"E372"),sQuery(id+"F0.wireOp",EDGE,"E374"),sQuery(id+"F0.wireOp",EDGE,"E376"),sQuery(id+"F0.wireOp",EDGE,"E377"),sQuery(id+"F0.wireOp",EDGE,"E378")])],"isStart":false}),makeQuery(id+"F1.opExtrude","CAP_FACE",FACE,{"disambiguationData":[OSD([sQuery(id+"F0.wireOp",EDGE,"E29"),sQuery(id+"F0.wireOp",EDGE,"E108"),sQuery(id+"F0.wireOp",EDGE,"E110"),sQuery(id+"F0.wireOp",EDGE,"E112"),sQuery(id+"F0.wireOp",EDGE,"E246"),sQuery(id+"F0.wireOp",EDGE,"E262"),sQuery(id+"F0.wireOp",EDGE,"E263"),sQuery(id+"F0.wireOp",EDGE,"E265"),sQuery(id+"F0.wireOp",EDGE,"E298"),sQuery(id+"F0.wireOp",EDGE,"E299"),sQuery(id+"F0.wireOp",EDGE,"E305"),sQuery(id+"F0.wireOp",EDGE,"E307"),sQuery(id+"F0.wireOp",EDGE,"E312"),sQuery(id+"F0.wireOp",EDGE,"E313"),sQuery(id+"F0.wireOp",EDGE,"E314"),sQuery(id+"F0.wireOp",EDGE,"E315"),sQuery(id+"F0.wireOp",EDGE,"E316"),sQuery(id+"F0.wireOp",EDGE,"E317"),sQuery(id+"F0.wireOp",EDGE,"E318"),sQuery(id+"F0.wireOp",EDGE,"E319"),sQuery(id+"F0.wireOp",EDGE,"E340"),sQuery(id+"F0.wireOp",EDGE,"E341")])],"isStart":false}),makeQuery(id+"F1.opExtrude","CAP_FACE",FACE,{"disambiguationData":[OSD([sQuery(id+"F0.wireOp",EDGE,"E32"),sQuery(id+"F0.wireOp",EDGE,"E33"),sQuery(id+"F0.wireOp",EDGE,"E34"),sQuery(id+"F0.wireOp",EDGE,"E35"),sQuery(id+"F0.wireOp",EDGE,"E36"),sQuery(id+"F0.wireOp",EDGE,"E37"),sQuery(id+"F0.wireOp",EDGE,"E38"),sQuery(id+"F0.wireOp",EDGE,"E39"),sQuery(id+"F0.wireOp",EDGE,"E40"),sQuery(id+"F0.wireOp",EDGE,"E41"),sQuery(id+"F0.wireOp",EDGE,"E42"),sQuery(id+"F0.wireOp",EDGE,"E43"),sQuery(id+"F0.wireOp",EDGE,"E44"),sQuery(id+"F0.wireOp",EDGE,"E45"),sQuery(id+"F0.wireOp",EDGE,"E69"),sQuery(id+"F0.wireOp",EDGE,"E70"),sQuery(id+"F0.wireOp",EDGE,"E98"),sQuery(id+"F0.wireOp",EDGE,"E99"),sQuery(id+"F0.wireOp",EDGE,"E100"),sQuery(id+"F0.wireOp",EDGE,"E101"),sQuery(id+"F0.wireOp",EDGE,"E102"),sQuery(id+"F0.wireOp",EDGE,"E103"),sQuery(id+"F0.wireOp",EDGE,"E104"),sQuery(id+"F0.wireOp",EDGE,"E105"),sQuery(id+"F0.wireOp",EDGE,"E194"),sQuery(id+"F0.wireOp",EDGE,"E205"),sQuery(id+"F0.wireOp",EDGE,"E254"),sQuery(id+"F0.wireOp",EDGE,"E257"),sQuery(id+"F0.wireOp",EDGE,"E46"),sQuery(id+"F0.wireOp",EDGE,"E270")])],"isStart":false}),makeQuery(id+"F1.opExtrude","CAP_FACE",FACE,{"disambiguationData":[OSD([sQuery(id+"F0.wireOp",EDGE,"E106"),sQuery(id+"F0.wireOp",EDGE,"E109"),sQuery(id+"F0.wireOp",EDGE,"E114"),sQuery(id+"F0.wireOp",EDGE,"E115"),sQuery(id+"F0.wireOp",EDGE,"E117"),sQuery(id+"F0.wireOp",EDGE,"E247"),sQuery(id+"F0.wireOp",EDGE,"E249"),sQuery(id+"F0.wireOp",EDGE,"E260"),sQuery(id+"F0.wireOp",EDGE,"E261"),sQuery(id+"F0.wireOp",EDGE,"E364"),sQuery(id+"F0.wireOp",EDGE,"E365"),sQuery(id+"F0.wireOp",EDGE,"E366"),sQuery(id+"F0.wireOp",EDGE,"E367"),sQuery(id+"F0.wireOp",EDGE,"E368")])],"isStart":false}),makeQuery(id+"F1.opExtrude","CAP_FACE",FACE,{"disambiguationData":[OSD([sQuery(id+"F0.wireOp",EDGE,"E118"),sQuery(id+"F0.wireOp",EDGE,"E242"),sQuery(id+"F0.wireOp",EDGE,"E245"),sQuery(id+"F0.wireOp",EDGE,"E264"),sQuery(id+"F0.wireOp",EDGE,"E303"),sQuery(id+"F0.wireOp",EDGE,"E308"),sQuery(id+"F0.wireOp",EDGE,"E310"),sQuery(id+"F0.wireOp",EDGE,"E311"),sQuery(id+"F0.wireOp",EDGE,"E329"),sQuery(id+"F0.wireOp",EDGE,"E331"),sQuery(id+"F0.wireOp",EDGE,"E332"),sQuery(id+"F0.wireOp",EDGE,"E333"),sQuery(id+"F0.wireOp",EDGE,"E334"),sQuery(id+"F0.wireOp",EDGE,"E335"),sQuery(id+"F0.wireOp",EDGE,"E336"),sQuery(id+"F0.wireOp",EDGE,"E337"),sQuery(id+"F0.wireOp",EDGE,"E338"),sQuery(id+"F0.wireOp",EDGE,"E347"),sQuery(id+"F0.wireOp",EDGE,"E348"),sQuery(id+"F0.wireOp",EDGE,"E349"),sQuery(id+"F0.wireOp",EDGE,"E350"),sQuery(id+"F0.wireOp",EDGE,"E351")])],"isStart":false}),makeQuery(id+"F1.opExtrude","CAP_FACE",FACE,{"disambiguationData":[OSD([sQuery(id+"F0.wireOp",EDGE,"E244"),sQuery(id+"F0.wireOp",EDGE,"E266"),sQuery(id+"F0.wireOp",EDGE,"E267"),sQuery(id+"F0.wireOp",EDGE,"E301"),sQuery(id+"F0.wireOp",EDGE,"E302"),sQuery(id+"F0.wireOp",EDGE,"E304"),sQuery(id+"F0.wireOp",EDGE,"E306"),sQuery(id+"F0.wireOp",EDGE,"E309"),sQuery(id+"F0.wireOp",EDGE,"E320"),sQuery(id+"F0.wireOp",EDGE,"E322"),sQuery(id+"F0.wireOp",EDGE,"E323"),sQuery(id+"F0.wireOp",EDGE,"E324"),sQuery(id+"F0.wireOp",EDGE,"E325"),sQuery(id+"F0.wireOp",EDGE,"E326"),sQuery(id+"F0.wireOp",EDGE,"E327"),sQuery(id+"F0.wireOp",EDGE,"E328"),sQuery(id+"F0.wireOp",EDGE,"E339"),sQuery(id+"F0.wireOp",EDGE,"E342"),sQuery(id+"F0.wireOp",EDGE,"E343"),sQuery(id+"F0.wireOp",EDGE,"E344"),sQuery(id+"F0.wireOp",EDGE,"E345"),sQuery(id+"F0.wireOp",EDGE,"E346")])],"isStart":false}),makeQuery(id+"F1.opExtrude","CAP_FACE",FACE,{"disambiguationData":[OSD([sQuery(id+"F0.wireOp",EDGE,"E252"),sQuery(id+"F0.wireOp",EDGE,"E273"),sQuery(id+"F0.wireOp",EDGE,"E274"),sQuery(id+"F0.wireOp",EDGE,"E400")])],"isStart":false}),makeQuery(id+"F7.opExtrude","CAP_FACE",FACE,{"disambiguationData":[OSD([sQuery(id+"F6.wireOp",EDGE,"E418.0"),sQuery(id+"F6.wireOp",EDGE,"E418.1"),sQuery(id+"F6.wireOp",EDGE,"E419"),sQuery(id+"F6.wireOp",EDGE,"E420")])],"isStart":true}),makeQuery(id+"F7.opExtrude","CAP_FACE",FACE,{"disambiguationData":[OSD([sQuery(id+"F6.wireOp",EDGE,"E421.0"),sQuery(id+"F6.wireOp",EDGE,"E421.1"),sQuery(id+"F6.wireOp",EDGE,"E422"),sQuery(id+"F6.wireOp",EDGE,"E423")])],"isStart":true}),makeQuery(id+"F7.opExtrude","CAP_FACE",FACE,{"disambiguationData":[OSD([sQuery(id+"F6.wireOp",EDGE,"E424.0"),sQuery(id+"F6.wireOp",EDGE,"E424.1"),sQuery(id+"F6.wireOp",EDGE,"E427"),sQuery(id+"F6.wireOp",EDGE,"E428")])],"isStart":true}),makeQuery(id+"F7.opExtrude","CAP_FACE",FACE,{"disambiguationData":[OSD([sQuery(id+"F6.wireOp",EDGE,"E424.2"),sQuery(id+"F6.wireOp",EDGE,"E424.3"),sQuery(id+"F6.wireOp",EDGE,"E425"),sQuery(id+"F6.wireOp",EDGE,"E426")])],"isStart":true}),makeQuery(id+"F7.opExtrude","CAP_FACE",FACE,{"disambiguationData":[OSD([sQuery(id+"F6.wireOp",EDGE,"E429.0"),sQuery(id+"F6.wireOp",EDGE,"E429.1"),sQuery(id+"F6.wireOp",EDGE,"E431"),sQuery(id+"F6.wireOp",EDGE,"E430")])],"isStart":true}),makeQuery(id+"F7.opExtrude","CAP_FACE",FACE,{"disambiguationData":[OSD([sQuery(id+"F6.wireOp",EDGE,"E432.0"),sQuery(id+"F6.wireOp",EDGE,"E432.1"),sQuery(id+"F6.wireOp",EDGE,"E438.trimOffspring"),sQuery(id+"F6.wireOp",EDGE,"E439.trimOffspring")])],"isStart":true}),makeQuery(id+"F7.opExtrude","CAP_FACE",FACE,{"disambiguationData":[OSD([sQuery(id+"F6.wireOp",EDGE,"E432.4"),sQuery(id+"F6.wireOp",EDGE,"E432.5"),sQuery(id+"F6.wireOp",EDGE,"E434.trimOffspring"),sQuery(id+"F6.wireOp",EDGE,"E436.trimOffspring")])],"isStart":true}),makeQuery(id+"F7.opExtrude","CAP_FACE",FACE,{"disambiguationData":[OSD([sQuery(id+"F6.wireOp",EDGE,"E432.6"),sQuery(id+"F6.wireOp",EDGE,"E432.7"),sQuery(id+"F6.wireOp",EDGE,"E433"),sQuery(id+"F6.wireOp",EDGE,"E435.trimOffspring")])],"isStart":true}),makeQuery(id+"F7.opExtrude","CAP_FACE",FACE,{"disambiguationData":[OSD([sQuery(id+"F6.wireOp",EDGE,"E440.0"),sQuery(id+"F6.wireOp",EDGE,"E440.1"),sQuery(id+"F6.wireOp",EDGE,"aKIUIKbC-LfDw-anEG-GlUg-Idod0CX9qstm"),sQuery(id+"F6.wireOp",EDGE,"54qWp3Ts-dfAN-WFkv-ai7W-jSZTlYv0wTdC")])],"isStart":true}),makeQuery(id+"F7.opExtrude","CAP_FACE",FACE,{"disambiguationData":[OSD([sQuery(id+"F6.wireOp",EDGE,"E440.2"),sQuery(id+"F6.wireOp",EDGE,"E440.3"),sQuery(id+"F6.wireOp",EDGE,"E441"),sQuery(id+"F6.wireOp",EDGE,"E442")])],"isStart":true}),makeQuery(id+"F7.opExtrude","CAP_FACE",FACE,{"disambiguationData":[OSD([sQuery(id+"F6.wireOp",EDGE,"E440.4"),sQuery(id+"F6.wireOp",EDGE,"E440.5"),sQuery(id+"F6.wireOp",EDGE,"E443"),sQuery(id+"F6.wireOp",EDGE,"E444")])],"isStart":true})]});
            var sketch = newSketch(context, id + "F8", { "sketchPlane" : qUnion([Q0])});
            skLineSegment(sketch, "E446.bottom", {"start": v(-2613.96, -8209.58) * mm, "end": v(-1749.8, -8209.58) * mm});
            skLineSegment(sketch, "E446.top", {"start": v(-2613.96, -8336.67) * mm, "end": v(-1749.8, -8336.67) * mm});
            skLineSegment(sketch, "E446.left", {"start": v(-2613.96, -8209.58) * mm, "end": v(-2613.96, -8336.67) * mm});
            skLineSegment(sketch, "E446.right", {"start": v(-1749.8, -8209.58) * mm, "end": v(-1749.8, -8336.67) * mm});
            skLineSegment(sketch, "E447.bottom", {"start": v(-4215.2, -4422.5) * mm, "end": v(-3351.04, -4422.5) * mm});
            skLineSegment(sketch, "E447.top", {"start": v(-4215.2, -4549.58) * mm, "end": v(-3351.04, -4549.58) * mm});
            skLineSegment(sketch, "E447.left", {"start": v(-4215.2, -4422.5) * mm, "end": v(-4215.2, -4549.58) * mm});
            skLineSegment(sketch, "E447.right", {"start": v(-3351.04, -4422.5) * mm, "end": v(-3351.04, -4549.58) * mm});
            skLineSegment(sketch, "E448.bottom", {"start": v(-2613.96, -4422.5) * mm, "end": v(-1749.8, -4422.5) * mm});
            skLineSegment(sketch, "E448.top", {"start": v(-2613.96, -4549.58) * mm, "end": v(-1749.8, -4549.58) * mm});
            skLineSegment(sketch, "E448.left", {"start": v(-2613.96, -4422.5) * mm, "end": v(-2613.96, -4549.58) * mm});
            skLineSegment(sketch, "E448.right", {"start": v(-1749.8, -4422.5) * mm, "end": v(-1749.8, -4549.58) * mm});
            skLineSegment(sketch, "E449.bottom", {"start": v(931.67, -4422.5) * mm, "end": v(1795.83, -4422.5) * mm});
            skLineSegment(sketch, "E449.top", {"start": v(931.67, -4549.58) * mm, "end": v(1795.83, -4549.58) * mm});
            skLineSegment(sketch, "E449.left", {"start": v(931.67, -4422.5) * mm, "end": v(931.67, -4549.58) * mm});
            skLineSegment(sketch, "E449.right", {"start": v(1795.83, -4422.5) * mm, "end": v(1795.83, -4549.58) * mm});
            skLineSegment(sketch, "E450.bottom", {"start": v(1919.8, -2046.04) * mm, "end": v(2783.97, -2046.04) * mm});
            skLineSegment(sketch, "E450.top", {"start": v(1919.8, -2173.12) * mm, "end": v(2783.97, -2173.12) * mm});
            skLineSegment(sketch, "E450.left", {"start": v(1919.8, -2046.04) * mm, "end": v(1919.8, -2173.12) * mm});
            skLineSegment(sketch, "E450.right", {"start": v(2783.97, -2046.04) * mm, "end": v(2783.97, -2173.12) * mm});
            skLineSegment(sketch, "E451.bottom", {"start": v(2936.47, -2046.04) * mm, "end": v(3800.64, -2046.04) * mm});
            skLineSegment(sketch, "E451.top", {"start": v(2936.47, -2173.12) * mm, "end": v(3800.64, -2173.12) * mm});
            skLineSegment(sketch, "E451.left", {"start": v(2936.47, -2046.04) * mm, "end": v(2936.47, -2173.12) * mm});
            skLineSegment(sketch, "E451.right", {"start": v(3800.64, -2046.04) * mm, "end": v(3800.64, -2173.12) * mm});
            skLineSegment(sketch, "E452.bottom", {"start": v(3953.14, -2046.04) * mm, "end": v(4817.3, -2046.04) * mm});
            skLineSegment(sketch, "E452.top", {"start": v(3953.14, -2173.12) * mm, "end": v(4817.3, -2173.12) * mm});
            skLineSegment(sketch, "E452.left", {"start": v(3953.14, -2046.04) * mm, "end": v(3953.14, -2173.12) * mm});
            skLineSegment(sketch, "E452.right", {"start": v(4817.3, -2046.04) * mm, "end": v(4817.3, -2173.12) * mm});
            skLineSegment(sketch, "E453.bottom", {"start": v(-2830, -2033.33) * mm, "end": v(-1965.83, -2033.33) * mm});
            skLineSegment(sketch, "E453.top", {"start": v(-2830, -2160.42) * mm, "end": v(-1965.83, -2160.42) * mm});
            skLineSegment(sketch, "E453.left", {"start": v(-2830, -2033.33) * mm, "end": v(-2830, -2160.42) * mm});
            skLineSegment(sketch, "E453.right", {"start": v(-1965.83, -2033.33) * mm, "end": v(-1965.83, -2160.42) * mm});
            skLineSegment(sketch, "E454.bottom", {"start": v(-7303.33, -2033.33) * mm, "end": v(-6439.17, -2033.33) * mm});
            skLineSegment(sketch, "E454.top", {"start": v(-7303.33, -2160.42) * mm, "end": v(-6439.17, -2160.42) * mm});
            skLineSegment(sketch, "E454.left", {"start": v(-7303.33, -2033.33) * mm, "end": v(-7303.33, -2160.42) * mm});
            skLineSegment(sketch, "E454.right", {"start": v(-6439.17, -2033.33) * mm, "end": v(-6439.17, -2160.42) * mm});
            skLineSegment(sketch, "E455.bottom", {"start": v(-5371.67, -3380.42) * mm, "end": v(-5244.58, -3380.42) * mm});
            skLineSegment(sketch, "E455.top", {"start": v(-5371.67, -4244.58) * mm, "end": v(-5244.58, -4244.58) * mm});
            skLineSegment(sketch, "E455.left", {"start": v(-5371.67, -3380.42) * mm, "end": v(-5371.67, -4244.58) * mm});
            skLineSegment(sketch, "E455.right", {"start": v(-5244.58, -3380.42) * mm, "end": v(-5244.58, -4244.58) * mm});
            skLineSegment(sketch, "E456.bottom", {"start": v(-5371.67, -711.67) * mm, "end": v(-5244.58, -711.67) * mm});
            skLineSegment(sketch, "E456.top", {"start": v(-5371.67, -1575.83) * mm, "end": v(-5244.58, -1575.83) * mm});
            skLineSegment(sketch, "E456.left", {"start": v(-5371.67, -711.67) * mm, "end": v(-5371.67, -1575.83) * mm});
            skLineSegment(sketch, "E456.right", {"start": v(-5244.58, -711.67) * mm, "end": v(-5244.58, -1575.83) * mm});
            skLineSegment(sketch, "E457.bottom", {"start": v(-4024.58, -711.67) * mm, "end": v(-3897.5, -711.67) * mm});
            skLineSegment(sketch, "E457.top", {"start": v(-4024.58, -1575.83) * mm, "end": v(-3897.5, -1575.83) * mm});
            skLineSegment(sketch, "E457.left", {"start": v(-4024.58, -711.67) * mm, "end": v(-4024.58, -1575.83) * mm});
            skLineSegment(sketch, "E457.right", {"start": v(-3897.5, -711.67) * mm, "end": v(-3897.5, -1575.83) * mm});
            skLineSegment(sketch, "E458.bottom", {"start": v(-2830, 2490.83) * mm, "end": v(-1965.83, 2490.83) * mm});
            skLineSegment(sketch, "E458.top", {"start": v(-2830, 2363.75) * mm, "end": v(-1965.83, 2363.75) * mm});
            skLineSegment(sketch, "E458.left", {"start": v(-2830, 2490.83) * mm, "end": v(-2830, 2363.75) * mm});
            skLineSegment(sketch, "E458.right", {"start": v(-1965.83, 2490.83) * mm, "end": v(-1965.83, 2363.75) * mm});
            skLineSegment(sketch, "E459.bottom", {"start": v(-7303.33, 2490.83) * mm, "end": v(-6439.17, 2490.83) * mm});
            skLineSegment(sketch, "E459.top", {"start": v(-7303.33, 2363.75) * mm, "end": v(-6439.17, 2363.75) * mm});
            skLineSegment(sketch, "E459.left", {"start": v(-7303.33, 2490.83) * mm, "end": v(-7303.33, 2363.75) * mm});
            skLineSegment(sketch, "E459.right", {"start": v(-6439.17, 2490.83) * mm, "end": v(-6439.17, 2363.75) * mm});
            skLineSegment(sketch, "E460.bottom", {"start": v(-5371.67, 3812.5) * mm, "end": v(-5244.58, 3812.5) * mm});
            skLineSegment(sketch, "E460.top", {"start": v(-5371.67, 2948.33) * mm, "end": v(-5244.58, 2948.33) * mm});
            skLineSegment(sketch, "E460.left", {"start": v(-5371.67, 3812.5) * mm, "end": v(-5371.67, 2948.33) * mm});
            skLineSegment(sketch, "E460.right", {"start": v(-5244.58, 3812.5) * mm, "end": v(-5244.58, 2948.33) * mm});
            skLineSegment(sketch, "E461.bottom", {"start": v(-4024.58, 3812.5) * mm, "end": v(-3897.5, 3812.5) * mm});
            skLineSegment(sketch, "E461.top", {"start": v(-4024.58, 2948.33) * mm, "end": v(-3897.5, 2948.33) * mm});
            skLineSegment(sketch, "E461.left", {"start": v(-4024.58, 3812.5) * mm, "end": v(-4024.58, 2948.33) * mm});
            skLineSegment(sketch, "E461.right", {"start": v(-3897.5, 3812.5) * mm, "end": v(-3897.5, 2948.33) * mm});
            skLineSegment(sketch, "E462.bottom", {"start": v(-7303.33, 7015) * mm, "end": v(-6439.17, 7015) * mm});
            skLineSegment(sketch, "E462.top", {"start": v(-7303.33, 6887.92) * mm, "end": v(-6439.17, 6887.92) * mm});
            skLineSegment(sketch, "E462.left", {"start": v(-7303.33, 7015) * mm, "end": v(-7303.33, 6887.92) * mm});
            skLineSegment(sketch, "E462.right", {"start": v(-6439.17, 7015) * mm, "end": v(-6439.17, 6887.92) * mm});
            skLineSegment(sketch, "E463.bottom", {"start": v(-2830, 7015) * mm, "end": v(-1965.83, 7015) * mm});
            skLineSegment(sketch, "E463.top", {"start": v(-2830, 6887.92) * mm, "end": v(-1965.83, 6887.92) * mm});
            skLineSegment(sketch, "E463.left", {"start": v(-2830, 7015) * mm, "end": v(-2830, 6887.92) * mm});
            skLineSegment(sketch, "E463.right", {"start": v(-1965.83, 7015) * mm, "end": v(-1965.83, 6887.92) * mm});
            skLineSegment(sketch, "E464.bottom", {"start": v(-5371.67, 8311.25) * mm, "end": v(-5244.58, 8311.25) * mm});
            skLineSegment(sketch, "E464.top", {"start": v(-5371.67, 7447.08) * mm, "end": v(-5244.58, 7447.08) * mm});
            skLineSegment(sketch, "E464.left", {"start": v(-5371.67, 8311.25) * mm, "end": v(-5371.67, 7447.08) * mm});
            skLineSegment(sketch, "E464.right", {"start": v(-5244.58, 8311.25) * mm, "end": v(-5244.58, 7447.08) * mm});
            skLineSegment(sketch, "E465.bottom", {"start": v(-4024.58, 8311.25) * mm, "end": v(-3897.5, 8311.25) * mm});
            skLineSegment(sketch, "E465.top", {"start": v(-4024.58, 7447.08) * mm, "end": v(-3897.5, 7447.08) * mm});
            skLineSegment(sketch, "E465.left", {"start": v(-4024.58, 8311.25) * mm, "end": v(-4024.58, 7447.08) * mm});
            skLineSegment(sketch, "E465.right", {"start": v(-3897.5, 8311.25) * mm, "end": v(-3897.5, 7447.08) * mm});
            skLineSegment(sketch, "E466.bottom", {"start": v(5252.5, 8336.67) * mm, "end": v(6116.67, 8336.67) * mm});
            skLineSegment(sketch, "E466.top", {"start": v(5252.5, 8209.58) * mm, "end": v(6116.67, 8209.58) * mm});
            skLineSegment(sketch, "E466.left", {"start": v(5252.5, 8336.67) * mm, "end": v(5252.5, 8209.58) * mm});
            skLineSegment(sketch, "E466.right", {"start": v(6116.67, 8336.67) * mm, "end": v(6116.67, 8209.58) * mm});
            skLineSegment(sketch, "E467.bottom", {"start": v(1249.38, 11259.58) * mm, "end": v(1351.04, 11259.58) * mm});
            skLineSegment(sketch, "E467.top", {"start": v(1249.38, 10395.42) * mm, "end": v(1351.04, 10395.42) * mm});
            skLineSegment(sketch, "E467.left", {"start": v(1249.38, 11259.58) * mm, "end": v(1249.38, 10395.42) * mm});
            skLineSegment(sketch, "E467.right", {"start": v(1351.04, 11259.58) * mm, "end": v(1351.04, 10395.42) * mm});
            skLineSegment(sketch, "E468.bottom", {"start": v(1249.38, 10242.92) * mm, "end": v(1351.04, 10242.92) * mm});
            skLineSegment(sketch, "E468.top", {"start": v(1249.38, 9378.75) * mm, "end": v(1351.04, 9378.75) * mm});
            skLineSegment(sketch, "E468.left", {"start": v(1249.38, 10242.92) * mm, "end": v(1249.38, 9378.75) * mm});
            skLineSegment(sketch, "E468.right", {"start": v(1351.04, 10242.92) * mm, "end": v(1351.04, 9378.75) * mm});
            skLineSegment(sketch, "E469.bottom", {"start": v(-377.3, -2033.33) * mm, "end": v(1351.04, -2033.33) * mm});
            skLineSegment(sketch, "E469.top", {"start": v(-377.3, -2173.12) * mm, "end": v(1351.04, -2173.12) * mm});
            skLineSegment(sketch, "E469.left", {"start": v(-377.3, -2033.33) * mm, "end": v(-377.3, -2173.12) * mm});
            skLineSegment(sketch, "E469.right", {"start": v(1351.04, -2033.33) * mm, "end": v(1351.04, -2173.12) * mm});
            skLineSegment(sketch, "E470.bottom", {"start": v(6421.67, -3170.73) * mm, "end": v(6625, -3170.73) * mm});
            skLineSegment(sketch, "E470.top", {"start": v(6421.67, -4034.9) * mm, "end": v(6625, -4034.9) * mm});
            skLineSegment(sketch, "E470.left", {"start": v(6421.67, -3170.73) * mm, "end": v(6421.67, -4034.9) * mm});
            skLineSegment(sketch, "E470.right", {"start": v(6625, -3170.73) * mm, "end": v(6625, -4034.9) * mm});
            skSolve(sketch);
        }
        {
            var Q0;
            Q0 = qSketchRegion(id + "F8", true);
            extrude(context, id + "F9", {"entities" : qUnion([Q0]), "operationType" : NewBodyOperationType.ADD, "oppositeDirection" : true, "depth" : 1360 * mm, "offsetDistance" : 25 * mm});
        }
        {
            var Q0;
            Q0=makeQuery(id+"F3.opExtrude","CAP_FACE",FACE,{"disambiguationData":[OSD([sQuery(id+"F2.wireOp",EDGE,"E404.bottom"),sQuery(id+"F2.wireOp",EDGE,"E404.top"),sQuery(id+"F2.wireOp",EDGE,"E404.left"),sQuery(id+"F2.wireOp",EDGE,"E404.right"),sQuery(id+"F2.wireOp",EDGE,"E405.0"),sQuery(id+"F2.wireOp",EDGE,"E405.1"),sQuery(id+"F2.wireOp",EDGE,"E405.2"),sQuery(id+"F2.wireOp",EDGE,"E406.trimOffspring")])],"isStart":true});
            var sketch = newSketch(context, id + "F10", { "sketchPlane" : qUnion([Q0])});
            skLineSegment(sketch, "E471.bottom", {"start": v(6421.67, -10268.33) * mm, "end": v(3761.67, -10268.33) * mm});
            skLineSegment(sketch, "E471.top", {"start": v(6421.67, -6913.33) * mm, "end": v(3761.67, -6913.33) * mm});
            skLineSegment(sketch, "E471.left", {"start": v(6421.67, -10268.33) * mm, "end": v(6421.67, -6913.33) * mm});
            skLineSegment(sketch, "E471.right", {"start": v(3761.67, -10268.33) * mm, "end": v(3761.67, -6913.33) * mm});
            skSolve(sketch);
        }
        {
            var Q0;
            Q0 = qSketchRegion(id + "F10", true);
            extrude(context, id + "F11", {"entities" : qUnion([Q0]), "operationType" : NewBodyOperationType.ADD, "depth" : 1500 * mm, "offsetDistance" : 25 * mm});
        }
        {
            var Q0;
            Q0=makeQuery(id+"F11.opExtrude","CAP_FACE",FACE,{"disambiguationData":[OSD([sQuery(id+"F10.wireOp",EDGE,"E471.bottom"),sQuery(id+"F10.wireOp",EDGE,"E471.top"),sQuery(id+"F10.wireOp",EDGE,"E471.left"),sQuery(id+"F10.wireOp",EDGE,"E471.right")])],"isStart":false});
            var sketch = newSketch(context, id + "F12", { "sketchPlane" : qUnion([Q0])});
            skLineSegment(sketch, "E472.bottom", {"start": v(6271.67, -7063.33) * mm, "end": v(3911.67, -7063.33) * mm});
            skLineSegment(sketch, "E472.top", {"start": v(6271.67, -9368.33) * mm, "end": v(3911.67, -9368.33) * mm});
            skLineSegment(sketch, "E472.left", {"start": v(6271.67, -7063.33) * mm, "end": v(6271.67, -9368.33) * mm});
            skLineSegment(sketch, "E472.right", {"start": v(3911.67, -7063.33) * mm, "end": v(3911.67, -9368.33) * mm});
            skSolve(sketch);
        }
        {
            var Q0;
            Q0 = qSketchRegion(id + "F12", true);
            extrude(context, id + "F13", {"entities" : qUnion([Q0]), "operationType" : NewBodyOperationType.REMOVE, "oppositeDirection" : true, "depth" : 1400 * mm, "offsetDistance" : 25 * mm});
        }
        {
            var Q0;
            Q0=makeQuery(id+"F11.opExtrude","CAP_FACE",FACE,{"disambiguationData":[OSD([sQuery(id+"F10.wireOp",EDGE,"E471.bottom"),sQuery(id+"F10.wireOp",EDGE,"E471.top"),sQuery(id+"F10.wireOp",EDGE,"E471.left"),sQuery(id+"F10.wireOp",EDGE,"E471.right")])],"isStart":false});
            var sketch = newSketch(context, id + "F14", { "sketchPlane" : qUnion([Q0])});
            skLineSegment(sketch, "E473.bottom", {"start": v(4861.67, -9968.33) * mm, "end": v(4261.67, -9968.33) * mm});
            skLineSegment(sketch, "E473.top", {"start": v(4861.67, -9568.33) * mm, "end": v(4261.67, -9568.33) * mm});
            skLineSegment(sketch, "E473.left", {"start": v(4861.67, -9968.33) * mm, "end": v(4861.67, -9568.33) * mm});
            skLineSegment(sketch, "E473.right", {"start": v(4261.67, -9968.33) * mm, "end": v(4261.67, -9568.33) * mm});
            skLineSegment(sketch, "E474", {"start": v(4561.67, -9568.33) * mm, "end": v(4561.67, -9368.33) * mm, "construction": true});
            skLineSegment(sketch, "E475.0", {"start": v(4636.67, -9568.33) * mm, "end": v(4636.67, -9268.33) * mm, "construction": true});
            skLineSegment(sketch, "E476.0", {"start": v(4486.67, -9568.33) * mm, "end": v(4486.67, -9268.33) * mm, "construction": true});
            skLineSegment(sketch, "E477.bottom", {"start": v(5921.67, -9968.33) * mm, "end": v(5321.67, -9968.33) * mm});
            skLineSegment(sketch, "E477.top", {"start": v(5921.67, -9568.33) * mm, "end": v(5321.67, -9568.33) * mm});
            skLineSegment(sketch, "E477.left", {"start": v(5921.67, -9968.33) * mm, "end": v(5921.67, -9568.33) * mm});
            skLineSegment(sketch, "E477.right", {"start": v(5321.67, -9968.33) * mm, "end": v(5321.67, -9568.33) * mm});
            skSolve(sketch);
        }
        {
            var Q0;
            Q0 = qSketchRegion(id + "F14", true);
            extrude(context, id + "F15", {"entities" : qUnion([Q0]), "operationType" : NewBodyOperationType.REMOVE, "oppositeDirection" : true, "depth" : 200 * mm, "offsetDistance" : 25 * mm});
        }
        {
            var Q0;
            Q0=makeQuery(id+"F11.opExtrude","CAP_FACE",FACE,{"disambiguationData":[OSD([sQuery(id+"F10.wireOp",EDGE,"E471.bottom"),sQuery(id+"F10.wireOp",EDGE,"E471.top"),sQuery(id+"F10.wireOp",EDGE,"E471.left"),sQuery(id+"F10.wireOp",EDGE,"E471.right")])],"isStart":false});
            var sketch = newSketch(context, id + "F16", { "sketchPlane" : qUnion([Q0])});
            skLineSegment(sketch, "E478", {"start": v(4561.67, -9568.33) * mm, "end": v(4561.67, -9368.33) * mm, "construction": true});
            skLineSegment(sketch, "E479.bottom", {"start": v(4461.67, -9568.33) * mm, "end": v(4661.67, -9568.33) * mm});
            skLineSegment(sketch, "E479.top", {"start": v(4461.67, -9368.33) * mm, "end": v(4661.67, -9368.33) * mm});
            skLineSegment(sketch, "E479.left", {"start": v(4461.67, -9568.33) * mm, "end": v(4461.67, -9368.33) * mm});
            skLineSegment(sketch, "E479.right", {"start": v(4661.67, -9568.33) * mm, "end": v(4661.67, -9368.33) * mm});
            skPoint(sketch, "E479.middle", {"position": v(4561.67, -9468.33) * mm});
            skSolve(sketch);
        }
        {
            var Q0;
            Q0 = qSketchRegion(id + "F16", true);
            extrude(context, id + "F17", {"entities" : qUnion([Q0]), "operationType" : NewBodyOperationType.REMOVE, "oppositeDirection" : true, "depth" : 50 * mm, "offsetDistance" : 25 * mm});
        }
        {
            var Q0;
            Q0=makeQuery(id+"F13.boolean.opBoolean","COPY",FACE,{"derivedFrom":makeQuery(id+"F13.opExtrude","SWEPT_FACE",FACE,{"disambiguationData":[OSD([sQuery(id+"F12.wireOp",EDGE,"E472.right")])]})});
            var sketch = newSketch(context, id + "F18", { "sketchPlane" : qUnion([Q0])});
            skLineSegment(sketch, "E480.0", {"start": v(-7063.33, 1325) * mm, "end": v(-7263.33, 1325) * mm});
            skLineSegment(sketch, "E481.0", {"start": v(-7263.33, 1150) * mm, "end": v(-7263.33, 1325) * mm});
            skLineSegment(sketch, "E482.0", {"start": v(-7263.33, 1150) * mm, "end": v(-7463.33, 1150) * mm});
            skLineSegment(sketch, "E483.0", {"start": v(-7463.33, 975) * mm, "end": v(-7663.33, 975) * mm});
            skLineSegment(sketch, "E484.0", {"start": v(-7663.33, 800) * mm, "end": v(-7663.33, 975) * mm});
            skLineSegment(sketch, "E485.0", {"start": v(-7663.33, 800) * mm, "end": v(-7863.33, 800) * mm});
            skLineSegment(sketch, "E486", {"start": v(-7463.33, 975) * mm, "end": v(-7463.33, 1150) * mm});
            skLineSegment(sketch, "E487.0", {"start": v(-7863.33, 625) * mm, "end": v(-8063.33, 625) * mm});
            skLineSegment(sketch, "E488.0", {"start": v(-8063.33, 450) * mm, "end": v(-8063.33, 625) * mm});
            skLineSegment(sketch, "E489.0", {"start": v(-8063.33, 450) * mm, "end": v(-8263.33, 450) * mm});
            skLineSegment(sketch, "E490", {"start": v(-7863.33, 625) * mm, "end": v(-7863.33, 800) * mm});
            skLineSegment(sketch, "E491.0", {"start": v(-8263.33, 275) * mm, "end": v(-8463.33, 275) * mm});
            skLineSegment(sketch, "E492.0", {"start": v(-8463.33, 100) * mm, "end": v(-8463.33, 275) * mm});
            skLineSegment(sketch, "E493", {"start": v(-8263.33, 275) * mm, "end": v(-8263.33, 450) * mm});
            skLineSegment(sketch, "E494", {"start": v(-7063.33, 1325) * mm, "end": v(-7063.33, 100) * mm});
            skLineSegment(sketch, "E495", {"start": v(-7063.33, 100) * mm, "end": v(-8463.33, 100) * mm});
            skSolve(sketch);
        }
        {
            var Q0;
            Q0 = qSketchRegion(id + "F18", true);
            extrude(context, id + "F19", {"entities" : qUnion([Q0]), "operationType" : NewBodyOperationType.ADD, "depth" : 1180 * mm, "offsetDistance" : 25 * mm});
        }
        {
            var Q0;
            Q0=makeQuery(id+"F1.opExtrude","SWEPT_FACE",FACE,{"disambiguationData":[OSD([sQuery(id+"F0.wireOp",EDGE,"E16")])]});
            var sketch = newSketch(context, id + "F20", { "sketchPlane" : qUnion([Q0])});
            skLineSegment(sketch, "E496", {"start": v(-4422.5, 0) * mm, "end": v(-8336.67, 3400) * mm, "construction": true});
            skLineSegment(sketch, "E497.0", {"start": v(-4722.5, 521.18) * mm, "end": v(-4722.5, 260.6) * mm});
            skLineSegment(sketch, "E498.0", {"start": v(-5022.5, 781.78) * mm, "end": v(-5022.5, 521.18) * mm});
            skLineSegment(sketch, "E499", {"start": v(-4722.5, 260.6) * mm, "end": v(-4422.5, 260.6) * mm});
            skLineSegment(sketch, "E500", {"start": v(-5022.5, 521.18) * mm, "end": v(-4722.5, 521.18) * mm});
            skLineSegment(sketch, "E501", {"start": v(-5322.5, 781.78) * mm, "end": v(-5022.5, 781.78) * mm});
            skLineSegment(sketch, "E502", {"start": v(-4422.5, 260.6) * mm, "end": v(-4422.5, 0) * mm});
            skLineSegment(sketch, "E503.0", {"start": v(-5622.5, 1302.96) * mm, "end": v(-5622.5, 1042.37) * mm});
            skLineSegment(sketch, "E504.0", {"start": v(-5922.5, 1563.55) * mm, "end": v(-5922.5, 1302.96) * mm});
            skLineSegment(sketch, "E505", {"start": v(-5622.5, 1042.37) * mm, "end": v(-5322.5, 1042.37) * mm});
            skLineSegment(sketch, "E506", {"start": v(-5922.5, 1302.96) * mm, "end": v(-5622.5, 1302.96) * mm});
            skLineSegment(sketch, "E507", {"start": v(-6222.5, 1563.55) * mm, "end": v(-5922.5, 1563.55) * mm});
            skLineSegment(sketch, "E508", {"start": v(-5322.5, 1042.37) * mm, "end": v(-5322.5, 781.78) * mm});
            skLineSegment(sketch, "E509.0", {"start": v(-6522.5, 2084.73) * mm, "end": v(-6522.5, 1824.14) * mm});
            skLineSegment(sketch, "E510.0", {"start": v(-6822.5, 2345.33) * mm, "end": v(-6822.5, 2084.73) * mm});
            skLineSegment(sketch, "E511", {"start": v(-6522.5, 1824.14) * mm, "end": v(-6222.5, 1824.14) * mm});
            skLineSegment(sketch, "E512", {"start": v(-6822.5, 2084.73) * mm, "end": v(-6522.5, 2084.73) * mm});
            skLineSegment(sketch, "E513", {"start": v(-7122.5, 2345.33) * mm, "end": v(-6822.5, 2345.33) * mm});
            skLineSegment(sketch, "E514", {"start": v(-6222.5, 1824.14) * mm, "end": v(-6222.5, 1563.55) * mm});
            skLineSegment(sketch, "E515.0", {"start": v(-7422.5, 2866.51) * mm, "end": v(-7422.5, 2605.92) * mm});
            skLineSegment(sketch, "E516.0", {"start": v(-7722.5, 3127.1) * mm, "end": v(-7722.5, 2866.51) * mm});
            skLineSegment(sketch, "E517", {"start": v(-7422.5, 2605.92) * mm, "end": v(-7122.5, 2605.92) * mm});
            skLineSegment(sketch, "E518", {"start": v(-7722.5, 2866.51) * mm, "end": v(-7422.5, 2866.51) * mm});
            skLineSegment(sketch, "E519", {"start": v(-8022.5, 3127.1) * mm, "end": v(-7722.5, 3127.1) * mm});
            skLineSegment(sketch, "E520", {"start": v(-7122.5, 2605.92) * mm, "end": v(-7122.5, 2345.33) * mm});
            skLineSegment(sketch, "E521", {"start": v(-8022.5, 3400) * mm, "end": v(-8022.5, 3127.1) * mm});
            skLineSegment(sketch, "E522", {"start": v(-8209.58, 3400) * mm, "end": v(-8022.5, 3400) * mm});
            skLineSegment(sketch, "E523", {"start": v(-8209.58, 0) * mm, "end": v(-8209.58, 3400) * mm});
            skLineSegment(sketch, "E524", {"start": v(-8209.58, 0) * mm, "end": v(-4422.5, 0) * mm});
            skSolve(sketch);
        }
        {
            var Q0;
            Q0 = qSketchRegion(id + "F20", true);
            extrude(context, id + "F21", {"entities" : qUnion([Q0]), "operationType" : NewBodyOperationType.ADD, "endBound" : BoundingType.UP_TO_NEXT, "depth" : 25 * mm, "offsetDistance" : 25 * mm});
        }
        {
            var Q0;
            Q0=makeQuery(id+"F1.opExtrude","SWEPT_FACE",FACE,{"disambiguationData":[OSD([sQuery(id+"F0.wireOp",EDGE,"E26")])]});
            var sketch = newSketch(context, id + "F22", { "sketchPlane" : qUnion([Q0])});
            skLineSegment(sketch, "E525.0", {"start": v(3236.42, 3400) * mm, "end": v(3236.42, 0) * mm, "construction": true});
            skLineSegment(sketch, "E526.MirrorCS", {"start": v(3236.42, 260.6) * mm, "end": v(3236.42, 0) * mm});
            skLineSegment(sketch, "E527.MirrorCS", {"start": v(6236.42, 2866.51) * mm, "end": v(6236.42, 2605.92) * mm});
            skLineSegment(sketch, "E528.MirrorCS", {"start": v(6536.42, 2866.51) * mm, "end": v(6236.42, 2866.51) * mm});
            skLineSegment(sketch, "E529.MirrorCS", {"start": v(5336.42, 1824.14) * mm, "end": v(5036.42, 1824.14) * mm});
            skLineSegment(sketch, "E530.MirrorCS", {"start": v(7023.5, 3400) * mm, "end": v(6836.42, 3400) * mm});
            skLineSegment(sketch, "E531.MirrorCS", {"start": v(6536.42, 3127.1) * mm, "end": v(6536.42, 2866.51) * mm});
            skLineSegment(sketch, "E532.MirrorCS", {"start": v(4136.42, 1042.37) * mm, "end": v(4136.42, 781.78) * mm});
            skLineSegment(sketch, "E533.MirrorCS", {"start": v(5336.42, 2084.73) * mm, "end": v(5336.42, 1824.14) * mm});
            skLineSegment(sketch, "E534.MirrorCS", {"start": v(5636.42, 2345.33) * mm, "end": v(5636.42, 2084.73) * mm});
            skLineSegment(sketch, "E535.MirrorCS", {"start": v(3236.42, 0) * mm, "end": v(7150.58, 3400) * mm, "construction": true});
            skLineSegment(sketch, "E536.MirrorCS", {"start": v(3536.42, 521.18) * mm, "end": v(3536.42, 260.6) * mm});
            skLineSegment(sketch, "E537.MirrorCS", {"start": v(3836.42, 781.78) * mm, "end": v(3836.42, 521.18) * mm});
            skLineSegment(sketch, "E538.MirrorCS", {"start": v(3536.42, 260.6) * mm, "end": v(3236.42, 260.6) * mm});
            skLineSegment(sketch, "E539.MirrorCS", {"start": v(3836.42, 521.18) * mm, "end": v(3536.42, 521.18) * mm});
            skLineSegment(sketch, "E540.MirrorCS", {"start": v(4136.42, 781.78) * mm, "end": v(3836.42, 781.78) * mm});
            skLineSegment(sketch, "E541.MirrorCS", {"start": v(6836.42, 3127.1) * mm, "end": v(6536.42, 3127.1) * mm});
            skLineSegment(sketch, "E542.MirrorCS", {"start": v(4436.42, 1302.96) * mm, "end": v(4436.42, 1042.37) * mm});
            skLineSegment(sketch, "E543.MirrorCS", {"start": v(6836.42, 3400) * mm, "end": v(6836.42, 3127.1) * mm});
            skLineSegment(sketch, "E544.MirrorCS", {"start": v(5936.42, 2345.33) * mm, "end": v(5636.42, 2345.33) * mm});
            skLineSegment(sketch, "E545.MirrorCS", {"start": v(5936.42, 2605.92) * mm, "end": v(5936.42, 2345.33) * mm});
            skLineSegment(sketch, "E546.MirrorCS", {"start": v(6236.42, 2605.92) * mm, "end": v(5936.42, 2605.92) * mm});
            skLineSegment(sketch, "E547.MirrorCS", {"start": v(5636.42, 2084.73) * mm, "end": v(5336.42, 2084.73) * mm});
            skLineSegment(sketch, "E548.MirrorCS", {"start": v(5036.42, 1563.55) * mm, "end": v(4736.42, 1563.55) * mm});
            skLineSegment(sketch, "E549.MirrorCS", {"start": v(4736.42, 1302.96) * mm, "end": v(4436.42, 1302.96) * mm});
            skLineSegment(sketch, "E550.MirrorCS", {"start": v(5036.42, 1824.14) * mm, "end": v(5036.42, 1563.55) * mm});
            skLineSegment(sketch, "E551.MirrorCS", {"start": v(4436.42, 1042.37) * mm, "end": v(4136.42, 1042.37) * mm});
            skLineSegment(sketch, "E552.MirrorCS", {"start": v(4736.42, 1563.55) * mm, "end": v(4736.42, 1302.96) * mm});
            skLineSegment(sketch, "E553.MirrorCS", {"start": v(7023.5, 0) * mm, "end": v(3236.42, 0) * mm});
            skLineSegment(sketch, "E554.MirrorCS", {"start": v(7023.5, 0) * mm, "end": v(7023.5, 3400) * mm});
            skSolve(sketch);
        }
        {
            var Q0;
            Q0 = qSketchRegion(id + "F22", true);
            extrude(context, id + "F23", {"entities" : qUnion([Q0]), "operationType" : NewBodyOperationType.ADD, "endBound" : BoundingType.UP_TO_NEXT, "depth" : 25 * mm, "offsetDistance" : 25 * mm});
        }
        {
            var Q0;
            Q0=makeQuery(id+"F23.boolean.opBoolean","MERGE",FACE,{"derivedFrom":[makeQuery(id+"F21.boolean.opBoolean","MERGE",FACE,{"derivedFrom":[makeQuery(id+"F9.boolean.opBoolean","MERGE",FACE,{"derivedFrom":[makeQuery(id+"F7.boolean.opBoolean","MERGE",FACE,{"derivedFrom":[makeQuery(id+"F1.opExtrude","CAP_FACE",FACE,{"disambiguationData":[OSD([sQuery(id+"F0.wireOp",EDGE,"E0"),sQuery(id+"F0.wireOp",EDGE,"E4"),sQuery(id+"F0.wireOp",EDGE,"E248"),sQuery(id+"F0.wireOp",EDGE,"E250"),sQuery(id+"F0.wireOp",EDGE,"E258"),sQuery(id+"F0.wireOp",EDGE,"E259")])],"isStart":false}),makeQuery(id+"F1.opExtrude","CAP_FACE",FACE,{"disambiguationData":[OSD([sQuery(id+"F0.wireOp",EDGE,"E1"),sQuery(id+"F0.wireOp",EDGE,"E25"),sQuery(id+"F0.wireOp",EDGE,"E26"),sQuery(id+"F0.wireOp",EDGE,"E27"),sQuery(id+"F0.wireOp",EDGE,"E47"),sQuery(id+"F0.wireOp",EDGE,"E68"),sQuery(id+"F0.wireOp",EDGE,"E120"),sQuery(id+"F0.wireOp",EDGE,"E121"),sQuery(id+"F0.wireOp",EDGE,"E122"),sQuery(id+"F0.wireOp",EDGE,"E123"),sQuery(id+"F0.wireOp",EDGE,"E124"),sQuery(id+"F0.wireOp",EDGE,"E125"),sQuery(id+"F0.wireOp",EDGE,"E126"),sQuery(id+"F0.wireOp",EDGE,"E132"),sQuery(id+"F0.wireOp",EDGE,"E133"),sQuery(id+"F0.wireOp",EDGE,"E139"),sQuery(id+"F0.wireOp",EDGE,"E174"),sQuery(id+"F0.wireOp",EDGE,"E175"),sQuery(id+"F0.wireOp",EDGE,"E176"),sQuery(id+"F0.wireOp",EDGE,"E177"),sQuery(id+"F0.wireOp",EDGE,"E178"),sQuery(id+"F0.wireOp",EDGE,"E179"),sQuery(id+"F0.wireOp",EDGE,"E180"),sQuery(id+"F0.wireOp",EDGE,"E182"),sQuery(id+"F0.wireOp",EDGE,"E183"),sQuery(id+"F0.wireOp",EDGE,"E184"),sQuery(id+"F0.wireOp",EDGE,"E185"),sQuery(id+"F0.wireOp",EDGE,"E186"),sQuery(id+"F0.wireOp",EDGE,"E187"),sQuery(id+"F0.wireOp",EDGE,"E188"),sQuery(id+"F0.wireOp",EDGE,"E189"),sQuery(id+"F0.wireOp",EDGE,"E190"),sQuery(id+"F0.wireOp",EDGE,"E191"),sQuery(id+"F0.wireOp",EDGE,"E192"),sQuery(id+"F0.wireOp",EDGE,"E193"),sQuery(id+"F0.wireOp",EDGE,"E206"),sQuery(id+"F0.wireOp",EDGE,"E207"),sQuery(id+"F0.wireOp",EDGE,"E208"),sQuery(id+"F0.wireOp",EDGE,"E209"),sQuery(id+"F0.wireOp",EDGE,"E210"),sQuery(id+"F0.wireOp",EDGE,"E211"),sQuery(id+"F0.wireOp",EDGE,"E212"),sQuery(id+"F0.wireOp",EDGE,"E213"),sQuery(id+"F0.wireOp",EDGE,"E243"),sQuery(id+"F0.wireOp",EDGE,"E256"),sQuery(id+"F0.wireOp",EDGE,"E268"),sQuery(id+"F0.wireOp",EDGE,"E269"),sQuery(id+"F0.wireOp",EDGE,"E277"),sQuery(id+"F0.wireOp",EDGE,"E278"),sQuery(id+"F0.wireOp",EDGE,"E279"),sQuery(id+"F0.wireOp",EDGE,"E281"),sQuery(id+"F0.wireOp",EDGE,"E282"),sQuery(id+"F0.wireOp",EDGE,"E283"),sQuery(id+"F0.wireOp",EDGE,"E284"),sQuery(id+"F0.wireOp",EDGE,"E285"),sQuery(id+"F0.wireOp",EDGE,"E286"),sQuery(id+"F0.wireOp",EDGE,"E287"),sQuery(id+"F0.wireOp",EDGE,"E288"),sQuery(id+"F0.wireOp",EDGE,"E290"),sQuery(id+"F0.wireOp",EDGE,"E291"),sQuery(id+"F0.wireOp",EDGE,"E292"),sQuery(id+"F0.wireOp",EDGE,"E293"),sQuery(id+"F0.wireOp",EDGE,"E294"),sQuery(id+"F0.wireOp",EDGE,"E295"),sQuery(id+"F0.wireOp",EDGE,"E296"),sQuery(id+"F0.wireOp",EDGE,"E352"),sQuery(id+"F0.wireOp",EDGE,"E353"),sQuery(id+"F0.wireOp",EDGE,"E354"),sQuery(id+"F0.wireOp",EDGE,"E355"),sQuery(id+"F0.wireOp",EDGE,"E356"),sQuery(id+"F0.wireOp",EDGE,"E357"),sQuery(id+"F0.wireOp",EDGE,"E358"),sQuery(id+"F0.wireOp",EDGE,"E359"),sQuery(id+"F0.wireOp",EDGE,"E360"),sQuery(id+"F0.wireOp",EDGE,"E361"),sQuery(id+"F0.wireOp",EDGE,"E362"),sQuery(id+"F0.wireOp",EDGE,"E363"),sQuery(id+"F0.wireOp",EDGE,"E402.trimOffspring")])],"isStart":false}),makeQuery(id+"F1.opExtrude","CAP_FACE",FACE,{"disambiguationData":[OSD([sQuery(id+"F0.wireOp",EDGE,"E2"),sQuery(id+"F0.wireOp",EDGE,"E5"),sQuery(id+"F0.wireOp",EDGE,"E127"),sQuery(id+"F0.wireOp",EDGE,"E128"),sQuery(id+"F0.wireOp",EDGE,"E129"),sQuery(id+"F0.wireOp",EDGE,"E130"),sQuery(id+"F0.wireOp",EDGE,"E253"),sQuery(id+"F0.wireOp",EDGE,"E255"),sQuery(id+"F0.wireOp",EDGE,"E271"),sQuery(id+"F0.wireOp",EDGE,"E272")])],"isStart":false}),makeQuery(id+"F1.opExtrude","CAP_FACE",FACE,{"disambiguationData":[OSD([sQuery(id+"F0.wireOp",EDGE,"E3"),sQuery(id+"F0.wireOp",EDGE,"E6"),sQuery(id+"F0.wireOp",EDGE,"E7"),sQuery(id+"F0.wireOp",EDGE,"E8"),sQuery(id+"F0.wireOp",EDGE,"E9"),sQuery(id+"F0.wireOp",EDGE,"E10"),sQuery(id+"F0.wireOp",EDGE,"E11"),sQuery(id+"F0.wireOp",EDGE,"E13"),sQuery(id+"F0.wireOp",EDGE,"E14"),sQuery(id+"F0.wireOp",EDGE,"E16"),sQuery(id+"F0.wireOp",EDGE,"E17"),sQuery(id+"F0.wireOp",EDGE,"E18"),sQuery(id+"F0.wireOp",EDGE,"E19"),sQuery(id+"F0.wireOp",EDGE,"E20"),sQuery(id+"F0.wireOp",EDGE,"E24"),sQuery(id+"F0.wireOp",EDGE,"E28"),sQuery(id+"F0.wireOp",EDGE,"E30"),sQuery(id+"F0.wireOp",EDGE,"E31"),sQuery(id+"F0.wireOp",EDGE,"E64"),sQuery(id+"F0.wireOp",EDGE,"E65"),sQuery(id+"F0.wireOp",EDGE,"E66"),sQuery(id+"F0.wireOp",EDGE,"E67"),sQuery(id+"F0.wireOp",EDGE,"E75"),sQuery(id+"F0.wireOp",EDGE,"E97"),sQuery(id+"F0.wireOp",EDGE,"E116"),sQuery(id+"F0.wireOp",EDGE,"E135"),sQuery(id+"F0.wireOp",EDGE,"E136"),sQuery(id+"F0.wireOp",EDGE,"E137"),sQuery(id+"F0.wireOp",EDGE,"E156"),sQuery(id+"F0.wireOp",EDGE,"E157"),sQuery(id+"F0.wireOp",EDGE,"E158"),sQuery(id+"F0.wireOp",EDGE,"E159"),sQuery(id+"F0.wireOp",EDGE,"E160"),sQuery(id+"F0.wireOp",EDGE,"E161"),sQuery(id+"F0.wireOp",EDGE,"E162"),sQuery(id+"F0.wireOp",EDGE,"E163"),sQuery(id+"F0.wireOp",EDGE,"E195"),sQuery(id+"F0.wireOp",EDGE,"E196"),sQuery(id+"F0.wireOp",EDGE,"E235"),sQuery(id+"F0.wireOp",EDGE,"E238"),sQuery(id+"F0.wireOp",EDGE,"E241"),sQuery(id+"F0.wireOp",EDGE,"E369"),sQuery(id+"F0.wireOp",EDGE,"E373"),sQuery(id+"F0.wireOp",EDGE,"E375")])],"isStart":false}),makeQuery(id+"F1.opExtrude","CAP_FACE",FACE,{"disambiguationData":[OSD([sQuery(id+"F0.wireOp",EDGE,"E15"),sQuery(id+"F0.wireOp",EDGE,"E76"),sQuery(id+"F0.wireOp",EDGE,"E77"),sQuery(id+"F0.wireOp",EDGE,"E78"),sQuery(id+"F0.wireOp",EDGE,"E79"),sQuery(id+"F0.wireOp",EDGE,"E80"),sQuery(id+"F0.wireOp",EDGE,"E81"),sQuery(id+"F0.wireOp",EDGE,"E82"),sQuery(id+"F0.wireOp",EDGE,"E83"),sQuery(id+"F0.wireOp",EDGE,"E84"),sQuery(id+"F0.wireOp",EDGE,"E85"),sQuery(id+"F0.wireOp",EDGE,"E86"),sQuery(id+"F0.wireOp",EDGE,"E87"),sQuery(id+"F0.wireOp",EDGE,"E88"),sQuery(id+"F0.wireOp",EDGE,"E89"),sQuery(id+"F0.wireOp",EDGE,"E90"),sQuery(id+"F0.wireOp",EDGE,"E91"),sQuery(id+"F0.wireOp",EDGE,"E92"),sQuery(id+"F0.wireOp",EDGE,"E93"),sQuery(id+"F0.wireOp",EDGE,"E94"),sQuery(id+"F0.wireOp",EDGE,"E95"),sQuery(id+"F0.wireOp",EDGE,"E96"),sQuery(id+"F0.wireOp",EDGE,"E131"),sQuery(id+"F0.wireOp",EDGE,"E134"),sQuery(id+"F0.wireOp",EDGE,"E164"),sQuery(id+"F0.wireOp",EDGE,"E165"),sQuery(id+"F0.wireOp",EDGE,"E166"),sQuery(id+"F0.wireOp",EDGE,"E167"),sQuery(id+"F0.wireOp",EDGE,"E168"),sQuery(id+"F0.wireOp",EDGE,"E169"),sQuery(id+"F0.wireOp",EDGE,"E170"),sQuery(id+"F0.wireOp",EDGE,"E171"),sQuery(id+"F0.wireOp",EDGE,"E172"),sQuery(id+"F0.wireOp",EDGE,"E173"),sQuery(id+"F0.wireOp",EDGE,"E275"),sQuery(id+"F0.wireOp",EDGE,"E276"),sQuery(id+"F0.wireOp",EDGE,"E401"),sQuery(id+"F0.wireOp",EDGE,"E403.trimOffspring")])],"isStart":false}),makeQuery(id+"F1.opExtrude","CAP_FACE",FACE,{"disambiguationData":[OSD([sQuery(id+"F0.wireOp",EDGE,"E21"),sQuery(id+"F0.wireOp",EDGE,"E22"),sQuery(id+"F0.wireOp",EDGE,"E23"),sQuery(id+"F0.wireOp",EDGE,"E71"),sQuery(id+"F0.wireOp",EDGE,"E72"),sQuery(id+"F0.wireOp",EDGE,"E73"),sQuery(id+"F0.wireOp",EDGE,"E74"),sQuery(id+"F0.wireOp",EDGE,"E113"),sQuery(id+"F0.wireOp",EDGE,"E251"),sQuery(id+"F0.wireOp",EDGE,"E370"),sQuery(id+"F0.wireOp",EDGE,"E371"),sQuery(id+"F0.wireOp",EDGE,"E372"),sQuery(id+"F0.wireOp",EDGE,"E374"),sQuery(id+"F0.wireOp",EDGE,"E376"),sQuery(id+"F0.wireOp",EDGE,"E377"),sQuery(id+"F0.wireOp",EDGE,"E378")])],"isStart":false}),makeQuery(id+"F1.opExtrude","CAP_FACE",FACE,{"disambiguationData":[OSD([sQuery(id+"F0.wireOp",EDGE,"E29"),sQuery(id+"F0.wireOp",EDGE,"E108"),sQuery(id+"F0.wireOp",EDGE,"E110"),sQuery(id+"F0.wireOp",EDGE,"E112"),sQuery(id+"F0.wireOp",EDGE,"E246"),sQuery(id+"F0.wireOp",EDGE,"E262"),sQuery(id+"F0.wireOp",EDGE,"E263"),sQuery(id+"F0.wireOp",EDGE,"E265"),sQuery(id+"F0.wireOp",EDGE,"E298"),sQuery(id+"F0.wireOp",EDGE,"E299"),sQuery(id+"F0.wireOp",EDGE,"E305"),sQuery(id+"F0.wireOp",EDGE,"E307"),sQuery(id+"F0.wireOp",EDGE,"E312"),sQuery(id+"F0.wireOp",EDGE,"E313"),sQuery(id+"F0.wireOp",EDGE,"E314"),sQuery(id+"F0.wireOp",EDGE,"E315"),sQuery(id+"F0.wireOp",EDGE,"E316"),sQuery(id+"F0.wireOp",EDGE,"E317"),sQuery(id+"F0.wireOp",EDGE,"E318"),sQuery(id+"F0.wireOp",EDGE,"E319"),sQuery(id+"F0.wireOp",EDGE,"E340"),sQuery(id+"F0.wireOp",EDGE,"E341")])],"isStart":false}),makeQuery(id+"F1.opExtrude","CAP_FACE",FACE,{"disambiguationData":[OSD([sQuery(id+"F0.wireOp",EDGE,"E32"),sQuery(id+"F0.wireOp",EDGE,"E33"),sQuery(id+"F0.wireOp",EDGE,"E34"),sQuery(id+"F0.wireOp",EDGE,"E35"),sQuery(id+"F0.wireOp",EDGE,"E36"),sQuery(id+"F0.wireOp",EDGE,"E37"),sQuery(id+"F0.wireOp",EDGE,"E38"),sQuery(id+"F0.wireOp",EDGE,"E39"),sQuery(id+"F0.wireOp",EDGE,"E40"),sQuery(id+"F0.wireOp",EDGE,"E41"),sQuery(id+"F0.wireOp",EDGE,"E42"),sQuery(id+"F0.wireOp",EDGE,"E43"),sQuery(id+"F0.wireOp",EDGE,"E44"),sQuery(id+"F0.wireOp",EDGE,"E45"),sQuery(id+"F0.wireOp",EDGE,"E69"),sQuery(id+"F0.wireOp",EDGE,"E70"),sQuery(id+"F0.wireOp",EDGE,"E98"),sQuery(id+"F0.wireOp",EDGE,"E99"),sQuery(id+"F0.wireOp",EDGE,"E100"),sQuery(id+"F0.wireOp",EDGE,"E101"),sQuery(id+"F0.wireOp",EDGE,"E102"),sQuery(id+"F0.wireOp",EDGE,"E103"),sQuery(id+"F0.wireOp",EDGE,"E104"),sQuery(id+"F0.wireOp",EDGE,"E105"),sQuery(id+"F0.wireOp",EDGE,"E194"),sQuery(id+"F0.wireOp",EDGE,"E205"),sQuery(id+"F0.wireOp",EDGE,"E254"),sQuery(id+"F0.wireOp",EDGE,"E257"),sQuery(id+"F0.wireOp",EDGE,"E46"),sQuery(id+"F0.wireOp",EDGE,"E270")])],"isStart":false}),makeQuery(id+"F1.opExtrude","CAP_FACE",FACE,{"disambiguationData":[OSD([sQuery(id+"F0.wireOp",EDGE,"E106"),sQuery(id+"F0.wireOp",EDGE,"E109"),sQuery(id+"F0.wireOp",EDGE,"E114"),sQuery(id+"F0.wireOp",EDGE,"E115"),sQuery(id+"F0.wireOp",EDGE,"E117"),sQuery(id+"F0.wireOp",EDGE,"E247"),sQuery(id+"F0.wireOp",EDGE,"E249"),sQuery(id+"F0.wireOp",EDGE,"E260"),sQuery(id+"F0.wireOp",EDGE,"E261"),sQuery(id+"F0.wireOp",EDGE,"E364"),sQuery(id+"F0.wireOp",EDGE,"E365"),sQuery(id+"F0.wireOp",EDGE,"E366"),sQuery(id+"F0.wireOp",EDGE,"E367"),sQuery(id+"F0.wireOp",EDGE,"E368")])],"isStart":false}),makeQuery(id+"F1.opExtrude","CAP_FACE",FACE,{"disambiguationData":[OSD([sQuery(id+"F0.wireOp",EDGE,"E118"),sQuery(id+"F0.wireOp",EDGE,"E242"),sQuery(id+"F0.wireOp",EDGE,"E245"),sQuery(id+"F0.wireOp",EDGE,"E264"),sQuery(id+"F0.wireOp",EDGE,"E303"),sQuery(id+"F0.wireOp",EDGE,"E308"),sQuery(id+"F0.wireOp",EDGE,"E310"),sQuery(id+"F0.wireOp",EDGE,"E311"),sQuery(id+"F0.wireOp",EDGE,"E329"),sQuery(id+"F0.wireOp",EDGE,"E331"),sQuery(id+"F0.wireOp",EDGE,"E332"),sQuery(id+"F0.wireOp",EDGE,"E333"),sQuery(id+"F0.wireOp",EDGE,"E334"),sQuery(id+"F0.wireOp",EDGE,"E335"),sQuery(id+"F0.wireOp",EDGE,"E336"),sQuery(id+"F0.wireOp",EDGE,"E337"),sQuery(id+"F0.wireOp",EDGE,"E338"),sQuery(id+"F0.wireOp",EDGE,"E347"),sQuery(id+"F0.wireOp",EDGE,"E348"),sQuery(id+"F0.wireOp",EDGE,"E349"),sQuery(id+"F0.wireOp",EDGE,"E350"),sQuery(id+"F0.wireOp",EDGE,"E351")])],"isStart":false}),makeQuery(id+"F1.opExtrude","CAP_FACE",FACE,{"disambiguationData":[OSD([sQuery(id+"F0.wireOp",EDGE,"E244"),sQuery(id+"F0.wireOp",EDGE,"E266"),sQuery(id+"F0.wireOp",EDGE,"E267"),sQuery(id+"F0.wireOp",EDGE,"E301"),sQuery(id+"F0.wireOp",EDGE,"E302"),sQuery(id+"F0.wireOp",EDGE,"E304"),sQuery(id+"F0.wireOp",EDGE,"E306"),sQuery(id+"F0.wireOp",EDGE,"E309"),sQuery(id+"F0.wireOp",EDGE,"E320"),sQuery(id+"F0.wireOp",EDGE,"E322"),sQuery(id+"F0.wireOp",EDGE,"E323"),sQuery(id+"F0.wireOp",EDGE,"E324"),sQuery(id+"F0.wireOp",EDGE,"E325"),sQuery(id+"F0.wireOp",EDGE,"E326"),sQuery(id+"F0.wireOp",EDGE,"E327"),sQuery(id+"F0.wireOp",EDGE,"E328"),sQuery(id+"F0.wireOp",EDGE,"E339"),sQuery(id+"F0.wireOp",EDGE,"E342"),sQuery(id+"F0.wireOp",EDGE,"E343"),sQuery(id+"F0.wireOp",EDGE,"E344"),sQuery(id+"F0.wireOp",EDGE,"E345"),sQuery(id+"F0.wireOp",EDGE,"E346")])],"isStart":false}),makeQuery(id+"F1.opExtrude","CAP_FACE",FACE,{"disambiguationData":[OSD([sQuery(id+"F0.wireOp",EDGE,"E252"),sQuery(id+"F0.wireOp",EDGE,"E273"),sQuery(id+"F0.wireOp",EDGE,"E274"),sQuery(id+"F0.wireOp",EDGE,"E400")])],"isStart":false}),makeQuery(id+"F7.opExtrude","CAP_FACE",FACE,{"disambiguationData":[OSD([sQuery(id+"F6.wireOp",EDGE,"E418.0"),sQuery(id+"F6.wireOp",EDGE,"E418.1"),sQuery(id+"F6.wireOp",EDGE,"E419"),sQuery(id+"F6.wireOp",EDGE,"E420")])],"isStart":true}),makeQuery(id+"F7.opExtrude","CAP_FACE",FACE,{"disambiguationData":[OSD([sQuery(id+"F6.wireOp",EDGE,"E421.0"),sQuery(id+"F6.wireOp",EDGE,"E421.1"),sQuery(id+"F6.wireOp",EDGE,"E422"),sQuery(id+"F6.wireOp",EDGE,"E423")])],"isStart":true}),makeQuery(id+"F7.opExtrude","CAP_FACE",FACE,{"disambiguationData":[OSD([sQuery(id+"F6.wireOp",EDGE,"E424.0"),sQuery(id+"F6.wireOp",EDGE,"E424.1"),sQuery(id+"F6.wireOp",EDGE,"E427"),sQuery(id+"F6.wireOp",EDGE,"E428")])],"isStart":true}),makeQuery(id+"F7.opExtrude","CAP_FACE",FACE,{"disambiguationData":[OSD([sQuery(id+"F6.wireOp",EDGE,"E424.2"),sQuery(id+"F6.wireOp",EDGE,"E424.3"),sQuery(id+"F6.wireOp",EDGE,"E425"),sQuery(id+"F6.wireOp",EDGE,"E426")])],"isStart":true}),makeQuery(id+"F7.opExtrude","CAP_FACE",FACE,{"disambiguationData":[OSD([sQuery(id+"F6.wireOp",EDGE,"E429.0"),sQuery(id+"F6.wireOp",EDGE,"E429.1"),sQuery(id+"F6.wireOp",EDGE,"E431"),sQuery(id+"F6.wireOp",EDGE,"E430")])],"isStart":true}),makeQuery(id+"F7.opExtrude","CAP_FACE",FACE,{"disambiguationData":[OSD([sQuery(id+"F6.wireOp",EDGE,"E432.0"),sQuery(id+"F6.wireOp",EDGE,"E432.1"),sQuery(id+"F6.wireOp",EDGE,"E438.trimOffspring"),sQuery(id+"F6.wireOp",EDGE,"E439.trimOffspring")])],"isStart":true}),makeQuery(id+"F7.opExtrude","CAP_FACE",FACE,{"disambiguationData":[OSD([sQuery(id+"F6.wireOp",EDGE,"E432.2"),sQuery(id+"F6.wireOp",EDGE,"E432.3"),sQuery(id+"F6.wireOp",EDGE,"E437.trimOffspring"),sQuery(id+"F6.wireOp",EDGE,"E445")])],"isStart":true}),makeQuery(id+"F7.opExtrude","CAP_FACE",FACE,{"disambiguationData":[OSD([sQuery(id+"F6.wireOp",EDGE,"E432.4"),sQuery(id+"F6.wireOp",EDGE,"E432.5"),sQuery(id+"F6.wireOp",EDGE,"E434.trimOffspring"),sQuery(id+"F6.wireOp",EDGE,"E436.trimOffspring")])],"isStart":true}),makeQuery(id+"F7.opExtrude","CAP_FACE",FACE,{"disambiguationData":[OSD([sQuery(id+"F6.wireOp",EDGE,"E432.6"),sQuery(id+"F6.wireOp",EDGE,"E432.7"),sQuery(id+"F6.wireOp",EDGE,"E433"),sQuery(id+"F6.wireOp",EDGE,"E435.trimOffspring")])],"isStart":true}),makeQuery(id+"F7.opExtrude","CAP_FACE",FACE,{"disambiguationData":[OSD([sQuery(id+"F6.wireOp",EDGE,"E440.2"),sQuery(id+"F6.wireOp",EDGE,"E440.3"),sQuery(id+"F6.wireOp",EDGE,"E441"),sQuery(id+"F6.wireOp",EDGE,"E442")])],"isStart":true}),makeQuery(id+"F7.opExtrude","CAP_FACE",FACE,{"disambiguationData":[OSD([sQuery(id+"F6.wireOp",EDGE,"E440.4"),sQuery(id+"F6.wireOp",EDGE,"E440.5"),sQuery(id+"F6.wireOp",EDGE,"E443"),sQuery(id+"F6.wireOp",EDGE,"E444")])],"isStart":true})]}),makeQuery(id+"F9.opExtrude","CAP_FACE",FACE,{"disambiguationData":[OSD([sQuery(id+"F8.wireOp",EDGE,"E446.bottom"),sQuery(id+"F8.wireOp",EDGE,"E446.top"),sQuery(id+"F8.wireOp",EDGE,"E446.left"),sQuery(id+"F8.wireOp",EDGE,"E446.right")])],"isStart":true}),makeQuery(id+"F9.opExtrude","CAP_FACE",FACE,{"disambiguationData":[OSD([sQuery(id+"F8.wireOp",EDGE,"E447.bottom"),sQuery(id+"F8.wireOp",EDGE,"E447.top"),sQuery(id+"F8.wireOp",EDGE,"E447.left"),sQuery(id+"F8.wireOp",EDGE,"E447.right")])],"isStart":true}),makeQuery(id+"F9.opExtrude","CAP_FACE",FACE,{"disambiguationData":[OSD([sQuery(id+"F8.wireOp",EDGE,"E448.bottom"),sQuery(id+"F8.wireOp",EDGE,"E448.top"),sQuery(id+"F8.wireOp",EDGE,"E448.left"),sQuery(id+"F8.wireOp",EDGE,"E448.right")])],"isStart":true}),makeQuery(id+"F9.opExtrude","CAP_FACE",FACE,{"disambiguationData":[OSD([sQuery(id+"F8.wireOp",EDGE,"E449.bottom"),sQuery(id+"F8.wireOp",EDGE,"E449.top"),sQuery(id+"F8.wireOp",EDGE,"E449.left"),sQuery(id+"F8.wireOp",EDGE,"E449.right")])],"isStart":true}),makeQuery(id+"F9.opExtrude","CAP_FACE",FACE,{"disambiguationData":[OSD([sQuery(id+"F8.wireOp",EDGE,"E450.bottom"),sQuery(id+"F8.wireOp",EDGE,"E450.top"),sQuery(id+"F8.wireOp",EDGE,"E450.left"),sQuery(id+"F8.wireOp",EDGE,"E450.right")])],"isStart":true}),makeQuery(id+"F9.opExtrude","CAP_FACE",FACE,{"disambiguationData":[OSD([sQuery(id+"F8.wireOp",EDGE,"E451.bottom"),sQuery(id+"F8.wireOp",EDGE,"E451.top"),sQuery(id+"F8.wireOp",EDGE,"E451.left"),sQuery(id+"F8.wireOp",EDGE,"E451.right")])],"isStart":true}),makeQuery(id+"F9.opExtrude","CAP_FACE",FACE,{"disambiguationData":[OSD([sQuery(id+"F8.wireOp",EDGE,"E452.bottom"),sQuery(id+"F8.wireOp",EDGE,"E452.top"),sQuery(id+"F8.wireOp",EDGE,"E452.left"),sQuery(id+"F8.wireOp",EDGE,"E452.right")])],"isStart":true}),makeQuery(id+"F9.opExtrude","CAP_FACE",FACE,{"disambiguationData":[OSD([sQuery(id+"F8.wireOp",EDGE,"E453.bottom"),sQuery(id+"F8.wireOp",EDGE,"E453.top"),sQuery(id+"F8.wireOp",EDGE,"E453.left"),sQuery(id+"F8.wireOp",EDGE,"E453.right")])],"isStart":true}),makeQuery(id+"F9.opExtrude","CAP_FACE",FACE,{"disambiguationData":[OSD([sQuery(id+"F8.wireOp",EDGE,"E454.bottom"),sQuery(id+"F8.wireOp",EDGE,"E454.top"),sQuery(id+"F8.wireOp",EDGE,"E454.left"),sQuery(id+"F8.wireOp",EDGE,"E454.right")])],"isStart":true}),makeQuery(id+"F9.opExtrude","CAP_FACE",FACE,{"disambiguationData":[OSD([sQuery(id+"F8.wireOp",EDGE,"E455.bottom"),sQuery(id+"F8.wireOp",EDGE,"E455.top"),sQuery(id+"F8.wireOp",EDGE,"E455.left"),sQuery(id+"F8.wireOp",EDGE,"E455.right")])],"isStart":true}),makeQuery(id+"F9.opExtrude","CAP_FACE",FACE,{"disambiguationData":[OSD([sQuery(id+"F8.wireOp",EDGE,"E456.bottom"),sQuery(id+"F8.wireOp",EDGE,"E456.top"),sQuery(id+"F8.wireOp",EDGE,"E456.left"),sQuery(id+"F8.wireOp",EDGE,"E456.right")])],"isStart":true}),makeQuery(id+"F9.opExtrude","CAP_FACE",FACE,{"disambiguationData":[OSD([sQuery(id+"F8.wireOp",EDGE,"E457.bottom"),sQuery(id+"F8.wireOp",EDGE,"E457.top"),sQuery(id+"F8.wireOp",EDGE,"E457.left"),sQuery(id+"F8.wireOp",EDGE,"E457.right")])],"isStart":true}),makeQuery(id+"F9.opExtrude","CAP_FACE",FACE,{"disambiguationData":[OSD([sQuery(id+"F8.wireOp",EDGE,"E458.bottom"),sQuery(id+"F8.wireOp",EDGE,"E458.top"),sQuery(id+"F8.wireOp",EDGE,"E458.left"),sQuery(id+"F8.wireOp",EDGE,"E458.right")])],"isStart":true}),makeQuery(id+"F9.opExtrude","CAP_FACE",FACE,{"disambiguationData":[OSD([sQuery(id+"F8.wireOp",EDGE,"E459.bottom"),sQuery(id+"F8.wireOp",EDGE,"E459.top"),sQuery(id+"F8.wireOp",EDGE,"E459.left"),sQuery(id+"F8.wireOp",EDGE,"E459.right")])],"isStart":true}),makeQuery(id+"F9.opExtrude","CAP_FACE",FACE,{"disambiguationData":[OSD([sQuery(id+"F8.wireOp",EDGE,"E460.bottom"),sQuery(id+"F8.wireOp",EDGE,"E460.top"),sQuery(id+"F8.wireOp",EDGE,"E460.left"),sQuery(id+"F8.wireOp",EDGE,"E460.right")])],"isStart":true}),makeQuery(id+"F9.opExtrude","CAP_FACE",FACE,{"disambiguationData":[OSD([sQuery(id+"F8.wireOp",EDGE,"E461.bottom"),sQuery(id+"F8.wireOp",EDGE,"E461.top"),sQuery(id+"F8.wireOp",EDGE,"E461.left"),sQuery(id+"F8.wireOp",EDGE,"E461.right")])],"isStart":true}),makeQuery(id+"F9.opExtrude","CAP_FACE",FACE,{"disambiguationData":[OSD([sQuery(id+"F8.wireOp",EDGE,"E462.bottom"),sQuery(id+"F8.wireOp",EDGE,"E462.top"),sQuery(id+"F8.wireOp",EDGE,"E462.left"),sQuery(id+"F8.wireOp",EDGE,"E462.right")])],"isStart":true}),makeQuery(id+"F9.opExtrude","CAP_FACE",FACE,{"disambiguationData":[OSD([sQuery(id+"F8.wireOp",EDGE,"E463.bottom"),sQuery(id+"F8.wireOp",EDGE,"E463.top"),sQuery(id+"F8.wireOp",EDGE,"E463.left"),sQuery(id+"F8.wireOp",EDGE,"E463.right")])],"isStart":true}),makeQuery(id+"F9.opExtrude","CAP_FACE",FACE,{"disambiguationData":[OSD([sQuery(id+"F8.wireOp",EDGE,"E464.bottom"),sQuery(id+"F8.wireOp",EDGE,"E464.top"),sQuery(id+"F8.wireOp",EDGE,"E464.left"),sQuery(id+"F8.wireOp",EDGE,"E464.right")])],"isStart":true}),makeQuery(id+"F9.opExtrude","CAP_FACE",FACE,{"disambiguationData":[OSD([sQuery(id+"F8.wireOp",EDGE,"E465.bottom"),sQuery(id+"F8.wireOp",EDGE,"E465.top"),sQuery(id+"F8.wireOp",EDGE,"E465.left"),sQuery(id+"F8.wireOp",EDGE,"E465.right")])],"isStart":true}),makeQuery(id+"F9.opExtrude","CAP_FACE",FACE,{"disambiguationData":[OSD([sQuery(id+"F8.wireOp",EDGE,"E466.bottom"),sQuery(id+"F8.wireOp",EDGE,"E466.top"),sQuery(id+"F8.wireOp",EDGE,"E466.left"),sQuery(id+"F8.wireOp",EDGE,"E466.right")])],"isStart":true}),makeQuery(id+"F9.opExtrude","CAP_FACE",FACE,{"disambiguationData":[OSD([sQuery(id+"F8.wireOp",EDGE,"E467.bottom"),sQuery(id+"F8.wireOp",EDGE,"E467.top"),sQuery(id+"F8.wireOp",EDGE,"E467.left"),sQuery(id+"F8.wireOp",EDGE,"E467.right")])],"isStart":true}),makeQuery(id+"F9.opExtrude","CAP_FACE",FACE,{"disambiguationData":[OSD([sQuery(id+"F8.wireOp",EDGE,"E468.bottom"),sQuery(id+"F8.wireOp",EDGE,"E468.top"),sQuery(id+"F8.wireOp",EDGE,"E468.left"),sQuery(id+"F8.wireOp",EDGE,"E468.right")])],"isStart":true}),makeQuery(id+"F9.opExtrude","CAP_FACE",FACE,{"disambiguationData":[OSD([sQuery(id+"F8.wireOp",EDGE,"E469.bottom"),sQuery(id+"F8.wireOp",EDGE,"E469.top"),sQuery(id+"F8.wireOp",EDGE,"E469.left"),sQuery(id+"F8.wireOp",EDGE,"E469.right")])],"isStart":true}),makeQuery(id+"F9.opExtrude","CAP_FACE",FACE,{"disambiguationData":[OSD([sQuery(id+"F8.wireOp",EDGE,"E470.bottom"),sQuery(id+"F8.wireOp",EDGE,"E470.top"),sQuery(id+"F8.wireOp",EDGE,"E470.left"),sQuery(id+"F8.wireOp",EDGE,"E470.right")])],"isStart":true})]}),makeQuery(id+"F21.opExtrude","SWEPT_FACE",FACE,{"disambiguationData":[OSD([sQuery(id+"F20.wireOp",EDGE,"E522")])]})]}),makeQuery(id+"F23.opExtrude","SWEPT_FACE",FACE,{"disambiguationData":[OSD([sQuery(id+"F22.wireOp",EDGE,"E530.MirrorCS")])]})]});
            var sketch = newSketch(context, id + "F24", { "sketchPlane" : qUnion([Q0])});
            skLineSegment(sketch, "E555", {"start": v(3405.76, -10471.67) * mm, "end": v(2744.93, -11488.33) * mm});
            skLineSegment(sketch, "E556", {"start": v(2744.93, -11488.33) * mm, "end": v(1100.9, -11488.33) * mm});
            skLineSegment(sketch, "E557", {"start": v(1100.9, -11488.33) * mm, "end": v(440.07, -10471.67) * mm});
            skLineSegment(sketch, "E558", {"start": v(3405.76, -10471.67) * mm, "end": v(3495.42, -10471.67) * mm});
            skLineSegment(sketch, "E559.0", {"start": v(3495.42, -9952.17) * mm, "end": v(3495.42, -10471.67) * mm});
            skLineSegment(sketch, "E560.0", {"start": v(350.42, -9952.17) * mm, "end": v(350.42, -10512.62) * mm});
            skLineSegment(sketch, "E561.0", {"start": v(350.42, -9952.17) * mm, "end": v(3495.42, -9952.17) * mm});
            skLineSegment(sketch, "E562", {"start": v(440.07, -10471.67) * mm, "end": v(350.42, -10512.62) * mm});
            skSolve(sketch);
        }
        {
            var Q0;
            Q0 = qSketchRegion(id + "F24", true);
            extrude(context, id + "F25", {"entities" : qUnion([Q0]), "operationType" : NewBodyOperationType.REMOVE, "oppositeDirection" : true, "depth" : 300 * mm, "offsetDistance" : 25 * mm});
        }
    });
